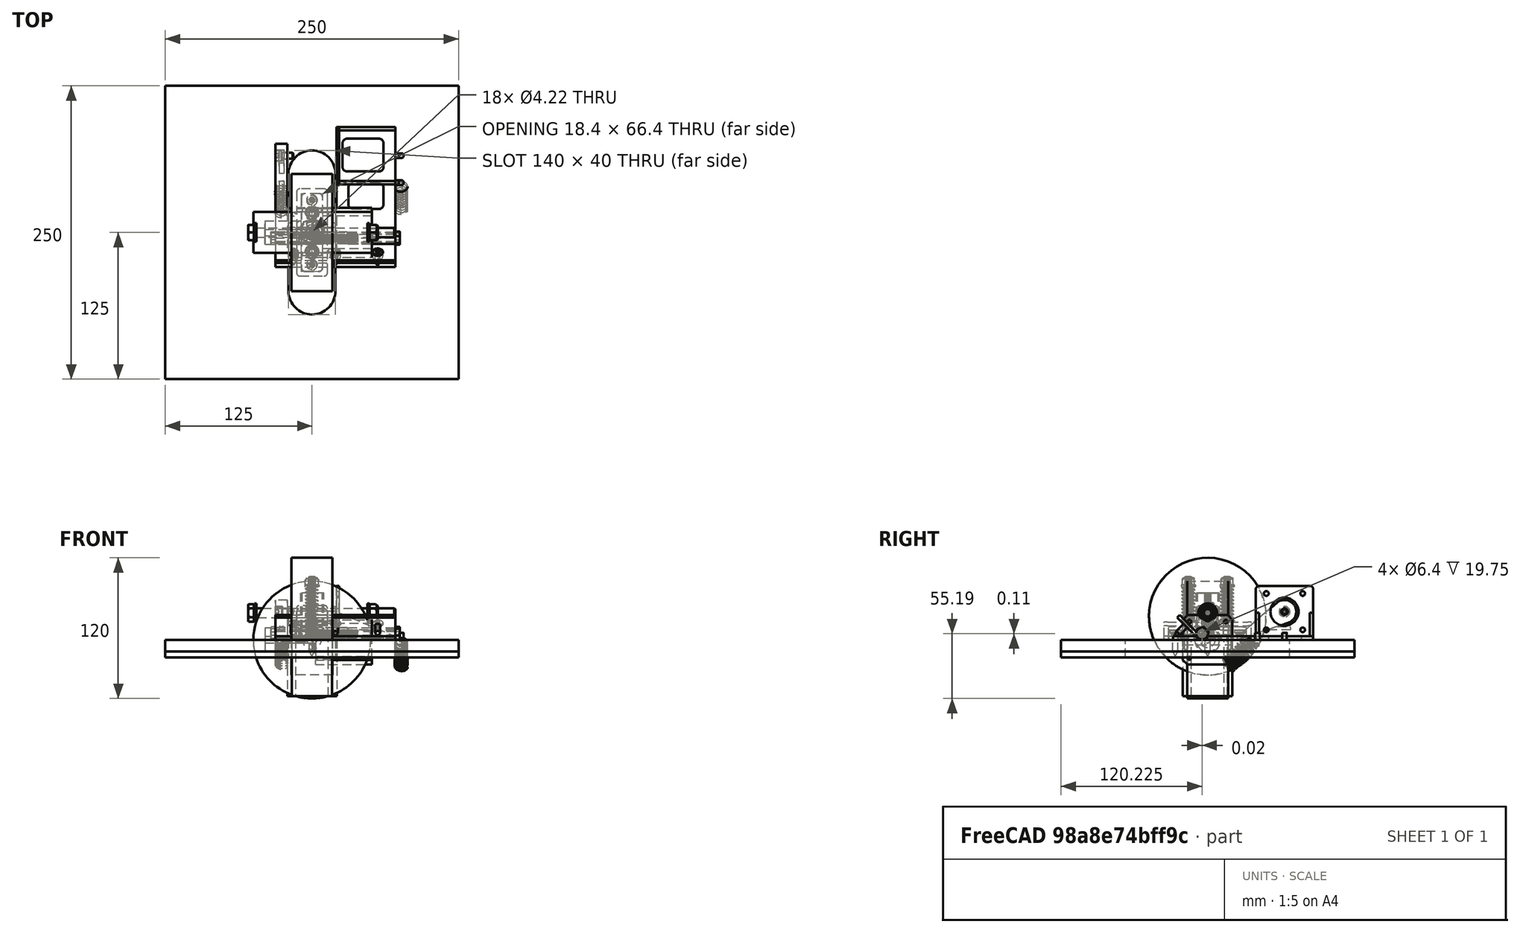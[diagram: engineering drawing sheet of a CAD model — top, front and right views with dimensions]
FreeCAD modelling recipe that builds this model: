
FCSTD DOCUMENT  (FreeCAD 1.0R39285 (Git))
Label: Stirnradantrieb
License: All rights reserved
LicenseURL: https://en.wikipedia.org/wiki/All_rights_reserved
objects: Sketcher::SketchObject×43, PartDesign::Pad×33, Part::FeaturePython×32, Part::Feature×17, PartDesign::Body×13, Mesh::Feature×9, App::Part×6, PartDesign::Pocket×5, PartDesign::Hole×4, PartDesign::Fillet×3, App::DocumentObjectGroup×3, PartDesign::Chamfer×1, App::FeaturePython×1, Assembly::JointGroup×1, PartDesign::AdditiveHelix×1, Assembly::AssemblyObject×1
note: 289 computed .brp shape members not serialized (recipe doc carries the construction recipe); baked Part::Feature solids carry a one-line shape summary decoded from their .brp

FEATURE [Sketcher::SketchObject] Sketch
  ArcFitTolerance = 1e-06
  AttachmentSupport = -> [XY_Plane]
  FullyConstrained = true
  MakeInternals = false
  MapMode = 5
  sketch-geometry (2):
    g0: Circle CenterX=0 CenterY=0 CenterZ=0 NormalX=0 NormalY=0 NormalZ=1 AngleXU=0 Radius=50
    g1: Circle CenterX=0 CenterY=0 CenterZ=0 NormalX=0 NormalY=0 NormalZ=1 AngleXU=0 Radius=4.2
  constraints (4):
    c: Diameter(g0) = 100
    c: Coincident(g0,g-1)
    c: Diameter(g1) = 8.4
    c: Coincident(g1,g0)
FEATURE [PartDesign::Pad] Pad
  Direction = (0,0,1)
  Length = 35
  Length2 = 10
  Midplane = true
  Profile = -> Sketch
  ReferenceAxis = -> Sketch [N_Axis]
  Refine = true
  Suppressed = false
  Type = 0
FEATURE [Sketcher::SketchObject] Sketch001
  ArcFitTolerance = 1e-06
  AttachmentSupport = -> [XY_Plane]
  ExternalGeometry = -> [Pad]
  FullyConstrained = true
  MakeInternals = false
  MapMode = 5
  sketch-geometry (2):
    g0: Circle CenterX=0 CenterY=0 CenterZ=0 NormalX=0 NormalY=0 NormalZ=1 AngleXU=0 Radius=8
    g1: Circle CenterX=0 CenterY=0 CenterZ=0 NormalX=0 NormalY=0 NormalZ=1 AngleXU=0 Radius=4.2
  constraints (4):
    c: Diameter(g0) = 16
    c: Coincident(g0,g-1)
    c: Coincident(g1,g0)
    c: Equal(g1,g-3)
FEATURE [PartDesign::Pad] Pad001
  BaseFeature = -> Pad
  Direction = (0,0,1)
  Length = 40
  Length2 = 10
  Midplane = true
  Profile = -> Sketch001
  ReferenceAxis = -> Sketch001 [N_Axis]
  Refine = true
  Suppressed = false
  Type = 0
FEATURE [PartDesign::Body] Body  label="B-Dummy Rad D100mm"
  AllowCompound = false
  Group = -> [Sketch,Pad,Sketch001,Pad001]
  Origin = -> Origin
  Placement = pos=(0,0,0) rot=(1,0,0;1.5708rad)
  Tip = -> Pad001
FEATURE [Sketcher::SketchObject] Sketch002  label="Sk-Walzenzylinder"
  ArcFitTolerance = 1e-06
  AttachmentSupport = -> [XY_Plane001]
  FullyConstrained = true
  MakeInternals = false
  MapMode = 5
  sketch-geometry (2):
    g0: Circle CenterX=0 CenterY=0 CenterZ=0 NormalX=0 NormalY=0 NormalZ=1 AngleXU=0 Radius=10
    g1: Circle CenterX=0 CenterY=0 CenterZ=0 NormalX=0 NormalY=0 NormalZ=1 AngleXU=0 Radius=2.65
  constraints (4):
    c: Diameter(g0) = 20
    c: Coincident(g0,g-1)
    c: Coincident(g1,g0)
    c: Diameter(g1) = 5.3
FEATURE [PartDesign::Pad] Pad002  label="P-Walzenzylinder"
  Direction = (0,0,1)
  Length = 40
  Length2 = 10
  Profile = -> Sketch002
  ReferenceAxis = -> Sketch002 [N_Axis]
  Refine = true
  Suppressed = false
  Type = 0
FEATURE [Sketcher::SketchObject] Sketch003  label="Sk-Wellenfeder"
  ArcFitTolerance = 1e-06
  AttachmentOffset = pos=(0,0,-5) rot=(0,0,1;0rad)
  AttachmentSupport = -> [Pad002]
  ExternalGeometry = -> [Pad002]
  FullyConstrained = true
  MakeInternals = false
  MapMode = 5
  Placement = pos=(0,0,5) rot=(1,0,0;3.14159rad)
  sketch-geometry (6):
    g0: LineSegment StartX=-1.67929 StartY=2.65 StartZ=0 EndX=-1.67929 EndY=2.05 EndZ=0
    g1: LineSegment StartX=-1.67929 StartY=2.05 StartZ=0 EndX=1.67929 EndY=2.05 EndZ=0
    g2: LineSegment StartX=1.67929 StartY=2.05 StartZ=0 EndX=1.67929 EndY=2.65 EndZ=0
    g3: LineSegment [constr] StartX=0 StartY=2.05 StartZ=0 EndX=0 EndY=-2.65 EndZ=0
    g4: LineSegment StartX=1.67929 StartY=2.65 StartZ=0 EndX=0 EndY=2.65 EndZ=0
    g5: LineSegment StartX=0 StartY=2.65 StartZ=0 EndX=-1.67929 EndY=2.65 EndZ=0
  constraints (19):
    c: Coincident(g0,g1)
    c: Coincident(g1,g2)
    c: Coincident(g2,g4)
    c: Coincident(g5,g0)
    c: Vertical(g0)
    c: Vertical(g2)
    c: Horizontal(g1)
    c: PointOnObject(g3,g-3)
    c: Vertical(g3)
    c: PointOnObject(g-1,g3)
    c: PointOnObject(g1,g-3)
    c: PointOnObject(g0,g-3)
    c: Coincident(g4,g5)
    c: Horizontal(g4)
    c: Horizontal(g5)
    c: PointOnObject(g4,g-3)
    c: Equal(g5,g4)
    c: PointOnObject(g3,g1)
    c: DistanceY(g3,g3) = 4.7
FEATURE [PartDesign::Pad] Pad003  label="P-Walze mit Wellenfeder"
  BaseFeature = -> Pad002
  Direction = (0,0,-1)
  Length = 20
  Length2 = 10
  Profile = -> Sketch003
  ReferenceAxis = -> Sketch003 [N_Axis]
  Refine = true
  Reversed = true
  Suppressed = false
  Type = 0
FEATURE [PartDesign::Chamfer] Chamfer  label="P-Antriebswalze NEMA17"
  Angle = 45
  Base = -> Pad003 [Edge13]
  BaseFeature = -> Pad003
  ChamferType = 0
  FlipDirection = false
  Refine = true
  Size = 0.5
  Size2 = 1
  SupportTransform = false
  Suppressed = false
  UseAllEdges = false
FEATURE [PartDesign::Body] Body001  label="B-Antriebswalze-NEMA17_20.0"
  AllowCompound = false
  Group = -> [Sketch002,Pad002,Sketch003,Pad003,Chamfer]
  Origin = -> Origin001
  Tip = -> Chamfer
FEATURE [Part::Feature] Body002  label="S-Dummy Rad D100"
  Placement = pos=(0.00966072,0.00966072,20) rot=(0.57735,-0.57735,0.57735;4.18879rad)
  shape: bbox 40 x 100 x 100 mm, 8 faces (baked)
FEATURE [Part::Feature] Body003  label="S-Antriebswalze-NEMA17"
  Placement = pos=(0,0,0) rot=(0,-1,0;1.5708rad)
  shape: bbox 40 x 20 x 20 mm, 8 faces (baked)
FEATURE [Sketcher::SketchObject] Sketch004  label="Sk-Stepper NEMA17 Body"
  ArcFitTolerance = 1e-06
  AttachmentSupport = -> [XY_Plane004]
  FullyConstrained = true
  MakeInternals = false
  MapMode = 5
  sketch-geometry (25):
    g0: LineSegment StartX=-21.15 StartY=17.15 StartZ=0 EndX=-21.15 EndY=-17.15 EndZ=0
    g1: LineSegment StartX=-17.15 StartY=-21.15 StartZ=0 EndX=17.15 EndY=-21.15 EndZ=0
    g2: LineSegment StartX=21.15 StartY=-17.15 StartZ=0 EndX=21.15 EndY=17.15 EndZ=0
    g3: LineSegment StartX=17.15 StartY=21.15 StartZ=0 EndX=-17.15 EndY=21.15 EndZ=0
    g4: LineSegment StartX=-21.15 StartY=17.15 StartZ=0 EndX=-17.15 EndY=21.15 EndZ=0
    g5: LineSegment StartX=17.15 StartY=21.15 StartZ=0 EndX=21.15 EndY=17.15 EndZ=0
    g6: LineSegment StartX=21.15 StartY=-17.15 StartZ=0 EndX=17.15 EndY=-21.15 EndZ=0
    g7: LineSegment StartX=-17.15 StartY=-21.15 StartZ=0 EndX=-21.15 EndY=-17.15 EndZ=0
    g8: LineSegment [constr] StartX=-21.15 StartY=17.15 StartZ=0 EndX=-17.15 EndY=17.15 EndZ=0
    g9: LineSegment [constr] StartX=-17.15 StartY=17.15 StartZ=0 EndX=-17.15 EndY=21.15 EndZ=0
    g10: LineSegment [constr] StartX=21.15 StartY=-17.15 StartZ=0 EndX=17.15 EndY=-17.15 EndZ=0
    g11: LineSegment [constr] StartX=17.15 StartY=-17.15 StartZ=0 EndX=17.15 EndY=-21.15 EndZ=0
    g12: LineSegment [constr] StartX=17.15 StartY=17.15 StartZ=0 EndX=21.15 EndY=17.15 EndZ=0
    g13: LineSegment [constr] StartX=17.15 StartY=17.15 StartZ=0 EndX=17.15 EndY=21.15 EndZ=0
    g14: LineSegment [constr] StartX=-17.15 StartY=-17.15 StartZ=0 EndX=-17.15 EndY=-21.15 EndZ=0
    g15: LineSegment [constr] StartX=-17.15 StartY=-17.15 StartZ=0 EndX=-21.15 EndY=-17.15 EndZ=0
    g16: LineSegment [constr] StartX=-15.5 StartY=-15.5 StartZ=0 EndX=15.5 EndY=-15.5 EndZ=0
    g17: LineSegment [constr] StartX=15.5 StartY=-15.5 StartZ=0 EndX=15.5 EndY=15.5 EndZ=0
    g18: LineSegment [constr] StartX=15.5 StartY=15.5 StartZ=0 EndX=-15.5 EndY=15.5 EndZ=0
    g19: LineSegment [constr] StartX=-15.5 StartY=15.5 StartZ=0 EndX=-15.5 EndY=-15.5 EndZ=0
    g20: GeomPoint [constr] X=0 Y=0 Z=0
    g21: Circle CenterX=-15.5 CenterY=15.5 CenterZ=0 NormalX=0 NormalY=0 NormalZ=1 AngleXU=0 Radius=1.5
    g22: Circle CenterX=15.5 CenterY=15.5 CenterZ=0 NormalX=0 NormalY=0 NormalZ=1 AngleXU=0 Radius=1.5
    g23: Circle CenterX=15.5 CenterY=-15.5 CenterZ=0 NormalX=0 NormalY=0 NormalZ=1 AngleXU=0 Radius=1.5
    g24: Circle CenterX=-15.5 CenterY=-15.5 CenterZ=0 NormalX=0 NormalY=0 NormalZ=1 AngleXU=0 Radius=1.5
  constraints (62):
    c: Vertical(g2)
    c: Horizontal(g1)
    c: Coincident(g4,g0)
    c: Coincident(g4,g3)
    c: Coincident(g5,g3)
    c: Coincident(g5,g2)
    c: Coincident(g6,g2)
    c: Coincident(g6,g1)
    c: Coincident(g7,g1)
    c: Coincident(g7,g0)
    c: Equal(g3,g2)
    c: Equal(g4,g5)
    c: Equal(g5,g6)
    c: Equal(g6,g7)
    c: DistanceX(g0,g2) = 42.3
    c: Coincident(g8,g0)
    c: Horizontal(g8)
    c: Coincident(g9,g8)
    c: Coincident(g9,g3)
    c: Coincident(g10,g2)
    c: Coincident(g11,g10)
    c: Coincident(g11,g1)
    c: Vertical(g11)
    c: Equal(g11,g10)
    c: Horizontal(g10)
    c: Equal(g8,g9)
    c: Vertical(g9)
    c: Coincident(g13,g3)
    c: Coincident(g14,g1)
    c: Coincident(g15,g0)
    c: Coincident(g12,g2)
    c: Vertical(g13)
    c: Vertical(g14)
    c: Coincident(g12,g13)
    c: Coincident(g14,g15)
    c: Horizontal(g15)
    c: Equal(g15,g14)
    c: Equal(g13,g12)
    c: Horizontal(g12)
    c: DistanceX(g8,g8) = 4
    c: Symmetric(g3,g3,g-2)
    c: Symmetric(g0,g0,g-1)
    c: Coincident(g16,g17)
    c: Coincident(g17,g18)
    c: Coincident(g18,g19)
    c: Coincident(g19,g16)
    c: Horizontal(g16)
    c: Horizontal(g18)
    c: Vertical(g17)
    c: Vertical(g19)
    c: Symmetric(g18,g16,g20)
    c: Coincident(g20,g-1)
    c: DistanceX(g18,g18) = 31
    c: Equal(g18,g17)
    c: Coincident(g21,g18)
    c: Coincident(g22,g17)
    c: Coincident(g23,g16)
    c: Coincident(g24,g16)
    c: Diameter(g21) = 3
    c: Equal(g21,g22)
    c: Equal(g22,g23)
    c: Equal(g23,g24)
FEATURE [PartDesign::Pad] Pad004  label="P-Stepper NEMA17 1"
  Direction = (0,0,1)
  Length = 48
  Length2 = 10
  Profile = -> Sketch004
  ReferenceAxis = -> Sketch004 [N_Axis]
  Refine = true
  Reversed = true
  Suppressed = false
  Type = 0
FEATURE [Sketcher::SketchObject] Sketch005  label="Sk-Stepper NEMA17 Centerring"
  ArcFitTolerance = 1e-06
  AttachmentSupport = -> [Pad004]
  FullyConstrained = true
  MakeInternals = false
  MapMode = 5
  sketch-geometry (2):
    g0: Circle CenterX=0 CenterY=0 CenterZ=0 NormalX=0 NormalY=0 NormalZ=1 AngleXU=0 Radius=6.5
    g1: Circle CenterX=0 CenterY=0 CenterZ=0 NormalX=0 NormalY=0 NormalZ=1 AngleXU=0 Radius=11
  constraints (4):
    c: Diameter(g0) = 13
    c: Coincident(g0,g-1)
    c: Diameter(g1) = 22
    c: Coincident(g1,g0)
FEATURE [PartDesign::Pad] Pad005  label="P-Stepper NEMA17 2"
  BaseFeature = -> Pad004
  Direction = (0,0,1)
  Length = 2
  Length2 = 10
  Profile = -> Sketch005
  ReferenceAxis = -> Sketch005 [N_Axis]
  Refine = true
  Suppressed = false
  Type = 0
FEATURE [Sketcher::SketchObject] Sketch006  label="Sk-Stepper NEMA17 Welle"
  ArcFitTolerance = 1e-06
  AttachmentSupport = -> [Pad005]
  FullyConstrained = true
  MakeInternals = false
  MapMode = 5
  sketch-geometry (1):
    g0: Circle CenterX=0 CenterY=0 CenterZ=0 NormalX=0 NormalY=0 NormalZ=1 AngleXU=0 Radius=2.5
  constraints (2):
    c: Diameter(g0) = 5
    c: Coincident(g0,g-1)
FEATURE [PartDesign::Pad] Pad006  label="P-Stepper NEMA17 dummy"
  BaseFeature = -> Pad005
  Direction = (0,0,1)
  Length = 24
  Length2 = 10
  Profile = -> Sketch006
  ReferenceAxis = -> Sketch006 [N_Axis]
  Refine = true
  Suppressed = false
  Type = 0
FEATURE [PartDesign::Body] Body004  label="B-Dummy Stepper NEMA17"
  AllowCompound = false
  Group = -> [Sketch004,Pad004,Sketch005,Pad005,Sketch006,Pad006]
  Origin = -> Origin004
  Tip = -> Pad006
FEATURE [Part::Feature] Body005  label="S-Dummy Stepper NEMA17"
  Placement = pos=(3,0,0) rot=(0,1,0;-1.5708rad)
  shape: bbox 72 x 42.3 x 42.3 mm, 20 faces (baked)
FEATURE [App::Part] Part  label="Stepper Antrieb"
  Group = -> [Body003,Body005]
  Origin = -> Origin005
  Placement = pos=(20,65.5,24.15) rot=(1,0,0;0rad)
FEATURE [Mesh::Feature] Mesh  label="M-Antriebswalze-NEMA17"
FEATURE [Sketcher::SketchObject] Sketch007  label="Sk Rotationsplatter"
  ArcFitTolerance = 1e-06
  AttachmentSupport = -> [XY_Plane006]
  FullyConstrained = true
  MakeInternals = false
  MapMode = 5
  sketch-geometry (8):
    g0: LineSegment StartX=-125 StartY=125 StartZ=0 EndX=-125 EndY=-125 EndZ=0
    g1: LineSegment StartX=-125 StartY=-125 StartZ=0 EndX=125 EndY=-125 EndZ=0
    g2: LineSegment StartX=125 StartY=-125 StartZ=0 EndX=125 EndY=125 EndZ=0
    g3: LineSegment StartX=125 StartY=125 StartZ=0 EndX=-125 EndY=125 EndZ=0
    g4: ArcOfCircle CenterX=0 CenterY=50 CenterZ=0 NormalX=0 NormalY=0 NormalZ=1 AngleXU=0 Radius=20 StartAngle=-9e-16 EndAngle=3.14159
    g5: ArcOfCircle CenterX=0 CenterY=-50 CenterZ=0 NormalX=0 NormalY=0 NormalZ=1 AngleXU=0 Radius=20 StartAngle=3.14159 EndAngle=6.28319
    g6: LineSegment StartX=20 StartY=50 StartZ=0 EndX=20 EndY=-50 EndZ=0
    g7: LineSegment StartX=-20 StartY=50 StartZ=0 EndX=-20 EndY=-50 EndZ=0
  constraints (20):
    c: Coincident(g0,g1)
    c: Coincident(g1,g2)
    c: Coincident(g2,g3)
    c: Coincident(g3,g0)
    c: Vertical(g0)
    c: Vertical(g2)
    c: Horizontal(g1)
    c: Horizontal(g3)
    c: Symmetric(g2,g0,g-1)
    c: DistanceY(g2,g2) = 250
    c: DistanceX(g3,g3) = 250
    c: Tangent(g4,g6) = 1.5708
    c: Tangent(g4,g7) = -1.5708
    c: Tangent(g5,g6) = 1.5708
    c: Tangent(g5,g7) = -1.5708
    c: Equal(g4,g5)
    c: PointOnObject(g4,g-2)
    c: Diameter(g4) = 40
    c: Symmetric(g4,g5,g-1)
    c: DistanceY(g5,g4) = 100
FEATURE [PartDesign::Pad] Pad007  label="P-Rotationsplatte"
  Direction = (0,0,1)
  Length = 15
  Length2 = 10
  Profile = -> Sketch007
  ReferenceAxis = -> Sketch007 [N_Axis]
  Refine = true
  Reversed = true
  Suppressed = false
  Type = 0
FEATURE [PartDesign::Body] Body006  label="B-Dummy Rotationsplatte"
  AllowCompound = false
  Group = -> [Sketch007,Pad007]
  Origin = -> Origin006
  Tip = -> Pad007
FEATURE [Sketcher::SketchObject] Sketch008  label="Sk Grundplatte"
  ArcFitTolerance = 1e-06
  AttachmentSupport = -> [XY_Plane008]
  FullyConstrained = true
  MakeInternals = false
  MapMode = 5
  sketch-geometry (5):
    g0: LineSegment StartX=-125 StartY=-125 StartZ=0 EndX=125 EndY=-125 EndZ=0
    g1: LineSegment StartX=125 StartY=-125 StartZ=0 EndX=125 EndY=125 EndZ=0
    g2: LineSegment StartX=125 StartY=125 StartZ=0 EndX=-125 EndY=125 EndZ=0
    g3: LineSegment StartX=-125 StartY=125 StartZ=0 EndX=-125 EndY=-125 EndZ=0
    g4: GeomPoint [constr] X=0 Y=0 Z=0
  constraints (12):
    c: Coincident(g0,g1)
    c: Coincident(g1,g2)
    c: Coincident(g2,g3)
    c: Coincident(g3,g0)
    c: Horizontal(g0)
    c: Horizontal(g2)
    c: Vertical(g1)
    c: Vertical(g3)
    c: Symmetric(g2,g0,g4)
    c: Distance(g1,g3) = 250
    c: Distance(g0,g2) = 250
    c: Coincident(g4,g-1)
FEATURE [PartDesign::Pad] Pad008
  Direction = (0,0,1)
  Length = 10
  Length2 = 10
  Profile = -> Sketch008
  ReferenceAxis = -> Sketch008 [N_Axis]
  Refine = true
  Reversed = true
  Suppressed = false
  Type = 0
FEATURE [PartDesign::Body] Body008  label="B-Dummy Grundplatte"
  AllowCompound = false
  Group = -> [Sketch008,Pad008]
  Origin = -> Origin008
  Tip = -> Pad008
FEATURE [Part::Feature] Body009  label="S-Dummy Grundplatte"
  shape: bbox 250 x 250 x 10 mm, 6 faces (baked)
FEATURE [Part::Feature] Body010  label="S-Dummy Rotationsplatte"
  shape: bbox 250 x 250 x 15 mm, 10 faces (baked)
FEATURE [Sketcher::SketchObject] Sketch009  label="Sk-Radlagerbasis Boden"
  ArcFitTolerance = 1e-06
  AttachmentSupport = -> [XY_Plane010]
  FullyConstrained = true
  MakeInternals = false
  MapMode = 5
  sketch-geometry (46):
    g0: LineSegment StartX=-9 StartY=30 StartZ=0 EndX=-9 EndY=-30 EndZ=0
    g1: LineSegment StartX=-6 StartY=-33 StartZ=0 EndX=6 EndY=-33 EndZ=0
    g2: LineSegment StartX=9 StartY=-30 StartZ=0 EndX=9 EndY=30 EndZ=0
    g3: LineSegment StartX=6 StartY=33 StartZ=0 EndX=-6 EndY=33 EndZ=0
    g4: ArcOfCircle CenterX=-6 CenterY=30 CenterZ=0 NormalX=0 NormalY=0 NormalZ=1 AngleXU=0 Radius=3 StartAngle=1.5708 EndAngle=3.14159
    g5: ArcOfCircle CenterX=-6 CenterY=-30 CenterZ=0 NormalX=0 NormalY=0 NormalZ=1 AngleXU=0 Radius=3 StartAngle=3.14159 EndAngle=4.71239
    g6: ArcOfCircle CenterX=6 CenterY=-30 CenterZ=0 NormalX=0 NormalY=0 NormalZ=1 AngleXU=0 Radius=3 StartAngle=4.71239 EndAngle=6.28319
    g7: ArcOfCircle CenterX=6 CenterY=30 CenterZ=0 NormalX=0 NormalY=0 NormalZ=1 AngleXU=0 Radius=3 StartAngle=0 EndAngle=1.5708
    g8: GeomPoint [constr] X=-9 Y=33 Z=0
    g9: GeomPoint [constr] X=9 Y=-33 Z=0
    g10: LineSegment StartX=3.00222 StartY=11.3 StartZ=0 EndX=6.00444 EndY=16.5 EndZ=0
    g11: LineSegment StartX=6.00444 StartY=16.5 StartZ=0 EndX=3.00222 EndY=21.7 EndZ=0
    g12: LineSegment StartX=3.00222 StartY=21.7 StartZ=0 EndX=-3.00222 EndY=21.7 EndZ=0
    g13: LineSegment StartX=-3.00222 StartY=21.7 StartZ=0 EndX=-6.00444 EndY=16.5 EndZ=0
    g14: LineSegment StartX=-6.00444 StartY=16.5 StartZ=0 EndX=-3.00222 EndY=11.3 EndZ=0
    g15: LineSegment StartX=-3.00222 StartY=11.3 StartZ=0 EndX=3.00222 EndY=11.3 EndZ=0
    g16: Circle [constr] CenterX=0 CenterY=16.5 CenterZ=0 NormalX=0 NormalY=0 NormalZ=1 AngleXU=0 Radius=6.00444
    g17: LineSegment StartX=-3.00222 StartY=-21.7 StartZ=0 EndX=3.00222 EndY=-21.7 EndZ=0
    g18: LineSegment StartX=3.00222 StartY=-21.7 StartZ=0 EndX=6.00444 EndY=-16.5 EndZ=0
    g19: LineSegment StartX=6.00444 StartY=-16.5 StartZ=0 EndX=3.00222 EndY=-11.3 EndZ=0
    g20: LineSegment StartX=3.00222 StartY=-11.3 StartZ=0 EndX=-3.00222 EndY=-11.3 EndZ=0
    g21: LineSegment StartX=-3.00222 StartY=-11.3 StartZ=0 EndX=-6.00444 EndY=-16.5 EndZ=0
    g22: LineSegment StartX=-6.00444 StartY=-16.5 StartZ=0 EndX=-3.00222 EndY=-21.7 EndZ=0
    g23: Circle [constr] CenterX=0 CenterY=-16.5 CenterZ=0 NormalX=0 NormalY=0 NormalZ=1 AngleXU=0 Radius=6.00444
    g24: LineSegment [constr] StartX=0 StartY=16.5 StartZ=0 EndX=0 EndY=-16.5 EndZ=0
    g25: Circle CenterX=0 CenterY=27.5 CenterZ=0 NormalX=0 NormalY=0 NormalZ=1 AngleXU=0 Radius=2.5
    g26: Circle CenterX=0 CenterY=-27.5 CenterZ=0 NormalX=0 NormalY=0 NormalZ=1 AngleXU=0 Radius=2.5
    g27: Circle CenterX=0 CenterY=0 CenterZ=0 NormalX=0 NormalY=0 NormalZ=1 AngleXU=0 Radius=2.5
    g28: LineSegment [constr] StartX=0 StartY=27.5 StartZ=0 EndX=0 EndY=30 EndZ=0
    g29: LineSegment [constr] StartX=0 StartY=30 StartZ=0 EndX=0 EndY=33 EndZ=0
    g30: LineSegment [constr] StartX=0 StartY=-27.5 StartZ=0 EndX=0 EndY=-30 EndZ=0
    g31: LineSegment [constr] StartX=0 StartY=-30 StartZ=0 EndX=0 EndY=-33 EndZ=0
    g32: Circle [constr] CenterX=0 CenterY=16.5 CenterZ=0 NormalX=0 NormalY=0 NormalZ=1 AngleXU=0 Radius=6.00444
    g33: Circle [constr] CenterX=0 CenterY=16.5 CenterZ=0 NormalX=0 NormalY=0 NormalZ=1 AngleXU=0 Radius=6.00444
    g34: Circle [constr] CenterX=0 CenterY=16.5 CenterZ=0 NormalX=0 NormalY=0 NormalZ=1 AngleXU=0 Radius=8.5
    g35: Circle [constr] CenterX=0 CenterY=-16.5 CenterZ=0 NormalX=0 NormalY=0 NormalZ=1 AngleXU=0 Radius=8.5
    g36: LineSegment [constr] StartX=-5 StartY=-8 StartZ=0 EndX=5 EndY=-8 EndZ=0
    g37: LineSegment [constr] StartX=5 StartY=-8 StartZ=0 EndX=5 EndY=8 EndZ=0
    g38: LineSegment [constr] StartX=5 StartY=8 StartZ=0 EndX=-5 EndY=8 EndZ=0
    g39: LineSegment [constr] StartX=-5 StartY=8 StartZ=0 EndX=-5 EndY=-8 EndZ=0
    g40: GeomPoint [constr] X=0 Y=0 Z=0
    g41: GeomPoint [constr] X=0 Y=25 Z=0
    g42: GeomPoint [constr] X=0 Y=8 Z=0
    g43: GeomPoint [constr] X=0 Y=-8 Z=0
    g44: GeomPoint [constr] X=0 Y=-25 Z=0
    g45: LineSegment [constr] StartX=-6.00444 StartY=16.5 StartZ=0 EndX=-9 EndY=16.5 EndZ=0
  constraints (112):
    c: Tangent(g0,g4) = -1.5708
    c: Tangent(g0,g5) = -1.5708
    c: Tangent(g1,g5) = -1.5708
    c: Tangent(g1,g6) = -1.5708
    c: Tangent(g2,g6) = -1.5708
    c: Tangent(g2,g7) = -1.5708
    c: Tangent(g3,g7) = -1.5708
    c: Tangent(g3,g4) = -1.5708
    c: Vertical(g0)
    c: Vertical(g2)
    c: Horizontal(g1)
    c: Horizontal(g3)
    c: Equal(g4,g5)
    c: Equal(g5,g6)
    c: Equal(g6,g7)
    c: PointOnObject(g8,g0)
    c: PointOnObject(g8,g3)
    c: PointOnObject(g9,g1)
    c: PointOnObject(g9,g2)
    c: Radius(g5) = 3
    c: Symmetric(g8,g9,g-1)
    c: DistanceX(g0,g2) = 18
    c: DistanceY(g1,g3) = 66
    c: Coincident(g10,g11)
    c: Coincident(g11,g12)
    c: Coincident(g12,g13)
    c: Coincident(g13,g14)
    c: Coincident(g14,g15)
    c: Coincident(g15,g10)
    c: Equal(g10, g11-g15) x5
    c: PointOnObject(g10,g16)
    c: PointOnObject(g12,g16)
    c: PointOnObject(g13,g16)
    c: PointOnObject(g14,g16)
    c: PointOnObject(g15,g16)
    c: PointOnObject(g16,g-2)
    c: Coincident(g17,g18)
    c: Coincident(g18,g19)
    c: Coincident(g19,g20)
    c: Coincident(g20,g21)
    c: Coincident(g21,g22)
    c: Coincident(g22,g17)
    c: Equal(g17, g18-g22) x5
    c: PointOnObject(g17,g23)
    c: PointOnObject(g18,g23)
    c: PointOnObject(g19,g23)
    c: PointOnObject(g20,g23)
    c: PointOnObject(g21,g23)
    c: Equal(g16,g23)
    c: Coincident(g24,g16)
    c: Coincident(g24,g23)
    c: Symmetric(g23,g16,g-1)
    c: Diameter(g25) = 5
    c: PointOnObject(g25,g-2)
    c: PointOnObject(g26,g-2)
    c: Coincident(g27,g-1)
    c: Equal(g25,g27)
    c: Equal(g27,g26)
    c: Coincident(g30,g26)
    c: PointOnObject(g31,g1)
    c: Coincident(g28,g29)
    c: Vertical(g28)
    c: Vertical(g29)
    c: PointOnObject(g28,g25)
    c: Coincident(g25,g28)
    c: DistanceY(g29,g29) = 3
    c: Coincident(g30,g31)
    c: Vertical(g30)
    c: Vertical(g31)
    c: PointOnObject(g30,g26)
    c: Equal(g31,g29)
    c: Coincident(g32,g16)
    c: PointOnObject(g10,g32)
    c: Coincident(g33,g16)
    c: PointOnObject(g10,g33)
    c: Coincident(g34,g16)
    c: Diameter(g34) = 17
    c: Coincident(g35,g23)
    c: Equal(g34,g35)
    c: Coincident(g36,g37)
    c: Coincident(g37,g38)
    c: Coincident(g38,g39)
    c: Coincident(g39,g36)
    c: Horizontal(g36)
    c: Horizontal(g38)
    c: Vertical(g37)
    c: Vertical(g39)
    c: Symmetric(g38,g36,g40)
    c: Distance(g37,g39) = 10
    c: Distance(g36,g38) = 16
    c: Coincident(g40,g27)
    c: PointOnObject(g41,g34)
    c: PointOnObject(g43,g35)
    c: PointOnObject(g44,g35)
    c: PointOnObject(g44,g26)
    c: PointOnObject(g44,g-2)
    c: PointOnObject(g41,g25)
    c: PointOnObject(g41,g-2)
    c: PointOnObject(g42,g34)
    c: PointOnObject(g42,g24)
    c: PointOnObject(g43,g24)
    c: PointOnObject(g42,g38)
    c: DistanceY(g11,g41) = 3.3
    c: PointOnObject(g11,g16)
    c: Horizontal(g12)
    c: DistanceY(g14,g12) = 10.4
    c: PointOnObject(g17,g23)
    c: Horizontal(g20)
    c: Coincident(g45,g13)
    c: PointOnObject(g45,g0)
    c: Horizontal(g45)
    c: DistanceX(g45,g45) = 2.99556
FEATURE [PartDesign::Pad] Pad009  label="P-Radlagerbasis 1"
  Direction = (0,0,1)
  Length = 4.2
  Length2 = 10
  Profile = -> Sketch009
  ReferenceAxis = -> Sketch009 [N_Axis]
  Refine = true
  Suppressed = false
  Type = 0
FEATURE [Sketcher::SketchObject] Sketch010  label="Sk-Radlagerbasis Deckel"
  ArcFitTolerance = 1e-06
  AttachmentSupport = -> [Pad009]
  ExternalGeometry = -> [Pad009]
  FullyConstrained = true
  MakeInternals = false
  MapMode = 5
  Placement = pos=(0,0,4.2) rot=(0,0,1;0rad)
  sketch-geometry (21):
    g0: LineSegment StartX=-9 StartY=30 StartZ=0 EndX=-9 EndY=-30 EndZ=0
    g1: LineSegment StartX=-6 StartY=-33 StartZ=0 EndX=6 EndY=-33 EndZ=0
    g2: LineSegment StartX=9 StartY=-30 StartZ=0 EndX=9 EndY=30 EndZ=0
    g3: LineSegment StartX=6 StartY=33 StartZ=0 EndX=-6 EndY=33 EndZ=0
    g4: ArcOfCircle CenterX=-6 CenterY=30 CenterZ=0 NormalX=0 NormalY=0 NormalZ=1 AngleXU=0 Radius=3 StartAngle=1.5708 EndAngle=3.14159
    g5: ArcOfCircle CenterX=-6 CenterY=-30 CenterZ=0 NormalX=0 NormalY=0 NormalZ=1 AngleXU=0 Radius=3 StartAngle=3.14159 EndAngle=4.71239
    g6: ArcOfCircle CenterX=6 CenterY=-30 CenterZ=0 NormalX=0 NormalY=0 NormalZ=1 AngleXU=0 Radius=3 StartAngle=4.71239 EndAngle=6.28319
    g7: ArcOfCircle CenterX=6 CenterY=30 CenterZ=0 NormalX=0 NormalY=0 NormalZ=1 AngleXU=0 Radius=3 StartAngle=3e-16 EndAngle=1.5708
    g8: GeomPoint [constr] X=-9 Y=33 Z=0
    g9: GeomPoint [constr] X=9 Y=-33 Z=0
    g10: Circle CenterX=0 CenterY=27.5 CenterZ=0 NormalX=0 NormalY=0 NormalZ=1 AngleXU=0 Radius=2.5
    g11: Circle CenterX=0 CenterY=0 CenterZ=0 NormalX=0 NormalY=0 NormalZ=1 AngleXU=0 Radius=2.5
    g12: Circle CenterX=0 CenterY=-27.5 CenterZ=0 NormalX=0 NormalY=0 NormalZ=1 AngleXU=0 Radius=2.5
    g13: LineSegment [constr] StartX=-3.00222 StartY=-11.3 StartZ=0 EndX=3.00222 EndY=-21.7 EndZ=0
    g14: LineSegment [constr] StartX=3.00222 StartY=-11.3 StartZ=0 EndX=-3.00222 EndY=-21.7 EndZ=0
    g15: LineSegment [constr] StartX=-3.00222 StartY=21.7 StartZ=0 EndX=3.00222 EndY=11.3 EndZ=0
    g16: LineSegment [constr] StartX=3.00222 StartY=21.7 StartZ=0 EndX=-3.00222 EndY=11.3 EndZ=0
    g17: GeomPoint [constr] X=-6e-16 Y=16.5 Z=0
    g18: GeomPoint [constr] X=5e-16 Y=-16.5 Z=0
    g19: Circle CenterX=-6e-16 CenterY=16.5 CenterZ=0 NormalX=0 NormalY=0 NormalZ=1 AngleXU=0 Radius=3.15
    g20: Circle CenterX=5e-16 CenterY=-16.5 CenterZ=0 NormalX=0 NormalY=0 NormalZ=1 AngleXU=0 Radius=3.15
  constraints (44):
    c: Tangent(g0,g4) = -1.5708
    c: Tangent(g0,g5) = -1.5708
    c: Tangent(g1,g5) = -1.5708
    c: Tangent(g1,g6) = -1.5708
    c: Tangent(g2,g6) = -1.5708
    c: Tangent(g2,g7) = -1.5708
    c: Tangent(g3,g7) = -1.5708
    c: Tangent(g3,g4) = -1.5708
    c: Vertical(g0)
    c: Vertical(g2)
    c: Horizontal(g1)
    c: Horizontal(g3)
    c: Equal(g4,g5)
    c: Equal(g5,g6)
    c: Equal(g6,g7)
    c: PointOnObject(g8,g0)
    c: PointOnObject(g8,g3)
    c: PointOnObject(g9,g1)
    c: PointOnObject(g9,g2)
    c: Coincident(g3,g-3)
    c: Equal(g4,g-3)
    c: Coincident(g1,g-7)
    c: Coincident(g10,g-4)
    c: Coincident(g11,g-1)
    c: Coincident(g12,g-6)
    c: Equal(g12,g-6)
    c: Equal(g11,g-5)
    c: Equal(g10,g-4)
    c: Coincident(g13,g-10)
    c: Coincident(g13,g-11)
    c: Coincident(g14,g-10)
    c: Coincident(g14,g-11)
    c: Coincident(g15,g-8)
    c: Coincident(g15,g-9)
    c: Coincident(g16,g-8)
    c: Coincident(g16,g-9)
    c: PointOnObject(g17,g15)
    c: PointOnObject(g18,g13)
    c: PointOnObject(g18,g14)
    c: PointOnObject(g17,g16)
    c: Diameter(g19) = 6.3
    c: Coincident(g19,g17)
    c: Coincident(g20,g18)
    c: Equal(g19,g20)
FEATURE [PartDesign::Pad] Pad010  label="P-Radlagerbasis 2"
  BaseFeature = -> Pad009
  Direction = (0,0,1)
  Length = 4
  Length2 = 10
  Profile = -> Sketch010
  ReferenceAxis = -> Sketch010 [N_Axis]
  Refine = true
  Suppressed = false
  Type = 0
FEATURE [Sketcher::SketchObject] Sketch011  label="Sk-Radlagerbasis Schraublöcher"
  ArcFitTolerance = 1e-06
  AttachmentSupport = -> [Pad010]
  ExternalGeometry = -> [Pad010]
  FullyConstrained = true
  MakeInternals = false
  MapMode = 5
  Placement = pos=(0,0,8.2) rot=(0,0,1;0rad)
  sketch-geometry (3):
    g0: Circle CenterX=0 CenterY=0 CenterZ=0 NormalX=0 NormalY=0 NormalZ=1 AngleXU=0 Radius=2.5
    g1: Circle CenterX=0 CenterY=-27.5 CenterZ=0 NormalX=0 NormalY=0 NormalZ=1 AngleXU=0 Radius=2.5
    g2: Circle CenterX=0 CenterY=27.5 CenterZ=0 NormalX=0 NormalY=0 NormalZ=1 AngleXU=0 Radius=2.5
  constraints (6):
    c: Coincident(g0,g-1)
    c: Coincident(g1,g-5)
    c: Equal(g1,g-5)
    c: Coincident(g2,g-4)
    c: Equal(g2,g-4)
    c: Equal(g-3,g0)
FEATURE [PartDesign::Hole] Hole  label="P-Radlagerbasis 3"
  BaseFeature = -> Pad010
  CustomThreadClearance = 0
  Depth = 2
  DepthType = 0
  Diameter = 9.2
  DrillForDepth = false
  DrillPoint = 1
  DrillPointAngle = 90
  HoleCutCountersinkAngle = 90
  HoleCutCustomValues = false
  HoleCutDepth = 0
  HoleCutDiameter = 15.8
  HoleCutType = 0
  ModelThread = false
  Profile = -> Sketch011
  Refine = true
  Suppressed = false
  Tapered = false
  TaperedAngle = 77
  ThreadClass = 0
  ThreadDepth = 2
  ThreadDepthType = 0
  ThreadDirection = 0
  ThreadFit = 0
  ThreadSize = 0
  ThreadType = 0
  Threaded = false
  UseCustomThreadClearance = false
FEATURE [PartDesign::Body] Body011  label="B-Radlagerbasis"
  AllowCompound = false
  Group = -> [Sketch009,Pad009,Sketch010,Pad010,Sketch011,Hole]
  Origin = -> Origin010
  Tip = -> Hole
FEATURE [Sketcher::SketchObject] Sketch015  label="Sk-Radlagerfeder Boden"
  ArcFitTolerance = 1e-06
  AttachmentSupport = -> [XY_Plane011]
  FullyConstrained = true
  MakeInternals = false
  MapMode = 5
  sketch-geometry (23):
    g0: LineSegment StartX=-9.2 StartY=30 StartZ=0 EndX=-9.2 EndY=-30 EndZ=0
    g1: LineSegment StartX=-6 StartY=-33.2 StartZ=0 EndX=6 EndY=-33.2 EndZ=0
    g2: LineSegment StartX=9.2 StartY=-30 StartZ=0 EndX=9.2 EndY=30 EndZ=0
    g3: LineSegment StartX=6 StartY=33.2 StartZ=0 EndX=-6 EndY=33.2 EndZ=0
    g4: ArcOfCircle CenterX=-6 CenterY=30 CenterZ=0 NormalX=0 NormalY=0 NormalZ=1 AngleXU=0 Radius=3.2 StartAngle=1.5708 EndAngle=3.14159
    g5: ArcOfCircle CenterX=-6 CenterY=-30 CenterZ=0 NormalX=0 NormalY=0 NormalZ=1 AngleXU=0 Radius=3.2 StartAngle=3.14159 EndAngle=4.71239
    g6: ArcOfCircle CenterX=6 CenterY=-30 CenterZ=0 NormalX=0 NormalY=0 NormalZ=1 AngleXU=0 Radius=3.2 StartAngle=4.71239 EndAngle=6.28319
    g7: ArcOfCircle CenterX=6 CenterY=30 CenterZ=0 NormalX=0 NormalY=0 NormalZ=1 AngleXU=0 Radius=3.2 StartAngle=0 EndAngle=1.5708
    g8: GeomPoint [constr] X=-9.2 Y=33.2 Z=0
    g9: GeomPoint [constr] X=9.2 Y=-33.2 Z=0
    g10: GeomPoint [constr] X=0 Y=0 Z=0
    g11: LineSegment StartX=-13.2 StartY=34.2 StartZ=0 EndX=-13.2 EndY=-34.2 EndZ=0
    g12: LineSegment StartX=-10.2 StartY=-37.2 StartZ=0 EndX=10.2 EndY=-37.2 EndZ=0
    g13: LineSegment StartX=13.2 StartY=-34.2 StartZ=0 EndX=13.2 EndY=34.2 EndZ=0
    g14: LineSegment StartX=10.2 StartY=37.2 StartZ=0 EndX=-10.2 EndY=37.2 EndZ=0
    g15: ArcOfCircle CenterX=-10.2 CenterY=34.2 CenterZ=0 NormalX=0 NormalY=0 NormalZ=1 AngleXU=0 Radius=3 StartAngle=1.5708 EndAngle=3.14159
    g16: ArcOfCircle CenterX=-10.2 CenterY=-34.2 CenterZ=0 NormalX=0 NormalY=0 NormalZ=1 AngleXU=0 Radius=3 StartAngle=3.14159 EndAngle=4.71239
    g17: ArcOfCircle CenterX=10.2 CenterY=-34.2 CenterZ=0 NormalX=0 NormalY=0 NormalZ=1 AngleXU=0 Radius=3 StartAngle=4.71239 EndAngle=6.28319
    g18: ArcOfCircle CenterX=10.2 CenterY=34.2 CenterZ=0 NormalX=0 NormalY=0 NormalZ=1 AngleXU=0 Radius=3 StartAngle=1e-16 EndAngle=1.5708
    g19: GeomPoint [constr] X=-13.2 Y=37.2 Z=0
    g20: GeomPoint [constr] X=13.2 Y=-37.2 Z=0
    g21: LineSegment [constr] StartX=-9.2 StartY=30 StartZ=0 EndX=-13.2 EndY=30 EndZ=0
    g22: LineSegment [constr] StartX=-6 StartY=33.2 StartZ=0 EndX=-6 EndY=37.2 EndZ=0
  constraints (53):
    c: Tangent(g0,g4) = -1.5708
    c: Tangent(g0,g5) = -1.5708
    c: Tangent(g1,g5) = -1.5708
    c: Tangent(g1,g6) = -1.5708
    c: Tangent(g2,g6) = -1.5708
    c: Tangent(g2,g7) = -1.5708
    c: Tangent(g3,g7) = -1.5708
    c: Tangent(g3,g4) = -1.5708
    c: Vertical(g0)
    c: Vertical(g2)
    c: Horizontal(g1)
    c: Horizontal(g3)
    c: Equal(g4,g5)
    c: Equal(g5,g6)
    c: Equal(g6,g7)
    c: PointOnObject(g8,g0)
    c: PointOnObject(g8,g3)
    c: PointOnObject(g9,g1)
    c: PointOnObject(g9,g2)
    c: Radius(g5) = 3.2
    c: Symmetric(g8,g9,g-1)
    c: DistanceX(g0,g2) = 18.4
    c: DistanceY(g1,g3) = 66.4
    c: Coincident(g-1,g10)
    c: Tangent(g11,g15) = -1.5708
    c: Tangent(g11,g16) = -1.5708
    c: Tangent(g12,g16) = -1.5708
    c: Tangent(g12,g17) = -1.5708
    c: Tangent(g13,g17) = -1.5708
    c: Tangent(g13,g18) = -1.5708
    c: Tangent(g14,g18) = -1.5708
    c: Tangent(g14,g15) = -1.5708
    c: Vertical(g11)
    c: Vertical(g13)
    c: Horizontal(g12)
    c: Horizontal(g14)
    c: Equal(g15,g16)
    c: Equal(g16,g17)
    c: Equal(g17,g18)
    c: PointOnObject(g19,g11)
    c: PointOnObject(g19,g14)
    c: PointOnObject(g20,g12)
    c: PointOnObject(g20,g13)
    c: Radius(g16) = 3
    c: Symmetric(g19,g20,g10)
    c: Coincident(g21,g0)
    c: PointOnObject(g21,g11)
    c: Horizontal(g21)
    c: DistanceX(g21,g21) = 4
    c: Coincident(g22,g3)
    c: PointOnObject(g22,g14)
    c: Vertical(g22)
    c: Equal(g21,g22)
FEATURE [PartDesign::Pad] Pad011  label="P-Radlagerfederung 1"
  Direction = (0,0,1)
  Length = 8
  Length2 = 10
  Profile = -> Sketch015
  ReferenceAxis = -> Sketch015 [N_Axis]
  Refine = true
  Suppressed = false
  Type = 0
FEATURE [Sketcher::SketchObject] Sketch016  label="Sk-Radlagerfeder Decke"
  ArcFitTolerance = 1e-06
  AttachmentSupport = -> [Pad011]
  ExternalGeometry = -> [Pad011]
  FullyConstrained = true
  MakeInternals = false
  MapMode = 5
  Placement = pos=(0,0,8) rot=(0,0,1;0rad)
  sketch-geometry (14):
    g0: LineSegment StartX=-13.2 StartY=34.2 StartZ=0 EndX=-13.2 EndY=-34.2 EndZ=0
    g1: LineSegment StartX=-10.2 StartY=-37.2 StartZ=0 EndX=10.2 EndY=-37.2 EndZ=0
    g2: LineSegment StartX=13.2 StartY=-34.2 StartZ=0 EndX=13.2 EndY=34.2 EndZ=0
    g3: LineSegment StartX=10.2 StartY=37.2 StartZ=0 EndX=-10.2 EndY=37.2 EndZ=0
    g4: ArcOfCircle CenterX=-10.2 CenterY=34.2 CenterZ=0 NormalX=0 NormalY=0 NormalZ=1 AngleXU=0 Radius=3 StartAngle=1.5708 EndAngle=3.14159
    g5: ArcOfCircle CenterX=-10.2 CenterY=-34.2 CenterZ=0 NormalX=0 NormalY=0 NormalZ=1 AngleXU=0 Radius=3 StartAngle=3.14159 EndAngle=4.71239
    g6: ArcOfCircle CenterX=10.2 CenterY=-34.2 CenterZ=0 NormalX=0 NormalY=0 NormalZ=1 AngleXU=0 Radius=3 StartAngle=4.71239 EndAngle=6.28319
    g7: ArcOfCircle CenterX=10.2 CenterY=34.2 CenterZ=0 NormalX=0 NormalY=0 NormalZ=1 AngleXU=0 Radius=3 StartAngle=4e-16 EndAngle=1.5708
    g8: GeomPoint [constr] X=-13.2 Y=37.2 Z=0
    g9: GeomPoint [constr] X=13.2 Y=-37.2 Z=0
    g10: LineSegment [constr] StartX=0 StartY=33.2 StartZ=0 EndX=0 EndY=16.5 EndZ=0
    g11: LineSegment [constr] StartX=0 StartY=16.5 StartZ=0 EndX=0 EndY=-16.5 EndZ=0
    g12: Circle CenterX=0 CenterY=16.5 CenterZ=0 NormalX=0 NormalY=0 NormalZ=1 AngleXU=0 Radius=3.2
    g13: Circle CenterX=0 CenterY=-16.5 CenterZ=0 NormalX=0 NormalY=0 NormalZ=1 AngleXU=0 Radius=3.2
  constraints (32):
    c: Tangent(g0,g4) = -1.5708
    c: Tangent(g0,g5) = -1.5708
    c: Tangent(g1,g5) = -1.5708
    c: Tangent(g1,g6) = -1.5708
    c: Tangent(g2,g6) = -1.5708
    c: Tangent(g2,g7) = -1.5708
    c: Tangent(g3,g7) = -1.5708
    c: Tangent(g3,g4) = -1.5708
    c: Vertical(g0)
    c: Vertical(g2)
    c: Horizontal(g1)
    c: Horizontal(g3)
    c: Equal(g4,g5)
    c: Equal(g5,g6)
    c: Equal(g6,g7)
    c: PointOnObject(g8,g0)
    c: PointOnObject(g8,g3)
    c: PointOnObject(g9,g1)
    c: PointOnObject(g9,g2)
    c: Equal(g4,g-3)
    c: Coincident(g3,g-3)
    c: Coincident(g1,g-4)
    c: Distance(g10) = 16.7
    c: PointOnObject(g10,g-5)
    c: Vertical(g10)
    c: PointOnObject(g10,g-2)
    c: Coincident(g11,g10)
    c: Symmetric(g11,g10,g-1)
    c: Diameter(g12) = 6.4
    c: Coincident(g12,g10)
    c: Coincident(g13,g11)
    c: Equal(g12,g13)
FEATURE [PartDesign::Pad] Pad012  label="P-Radlagerfederung 2"
  BaseFeature = -> Pad011
  Direction = (0,0,1)
  Length = 4
  Length2 = 10
  Profile = -> Sketch016
  ReferenceAxis = -> Sketch016 [N_Axis]
  Refine = true
  Suppressed = false
  Type = 0
FEATURE [Sketcher::SketchObject] Sketch017  label="Sk-Radlagerfeder Lager"
  ArcFitTolerance = 1e-06
  AttachmentSupport = -> [Pad012]
  ExternalGeometry = -> [Pad012]
  FullyConstrained = true
  MakeInternals = false
  MapMode = 5
  Placement = pos=(0,0,12) rot=(0,0,1;0rad)
  sketch-geometry (12):
    g0: Circle [constr] CenterX=0 CenterY=16.5 CenterZ=0 NormalX=0 NormalY=0 NormalZ=1 AngleXU=0 Radius=7
    g1: Circle [constr] CenterX=0 CenterY=-16.5 CenterZ=0 NormalX=0 NormalY=0 NormalZ=1 AngleXU=0 Radius=7
    g2: LineSegment StartX=-13.2 StartY=7 StartZ=0 EndX=-13.2 EndY=-7 EndZ=0
    g3: LineSegment StartX=-11.2 StartY=-9 StartZ=0 EndX=11.2 EndY=-9 EndZ=0
    g4: LineSegment StartX=13.2 StartY=-7 StartZ=0 EndX=13.2 EndY=7 EndZ=0
    g5: LineSegment StartX=11.2 StartY=9 StartZ=0 EndX=-11.2 EndY=9 EndZ=0
    g6: ArcOfCircle CenterX=-11.2 CenterY=7 CenterZ=0 NormalX=0 NormalY=0 NormalZ=1 AngleXU=0 Radius=2 StartAngle=1.5708 EndAngle=3.14159
    g7: ArcOfCircle CenterX=-11.2 CenterY=-7 CenterZ=0 NormalX=0 NormalY=0 NormalZ=1 AngleXU=0 Radius=2 StartAngle=3.14159 EndAngle=4.71239
    g8: ArcOfCircle CenterX=11.2 CenterY=-7 CenterZ=0 NormalX=0 NormalY=0 NormalZ=1 AngleXU=0 Radius=2 StartAngle=4.71239 EndAngle=6.28319
    g9: ArcOfCircle CenterX=11.2 CenterY=7 CenterZ=0 NormalX=0 NormalY=0 NormalZ=1 AngleXU=0 Radius=2 StartAngle=2e-16 EndAngle=1.5708
    g10: GeomPoint [constr] X=-13.2 Y=9 Z=0
    g11: GeomPoint [constr] X=13.2 Y=-9 Z=0
  constraints (27):
    c: Diameter(g0) = 14
    c: Coincident(g0,g-5)
    c: Coincident(g1,g-6)
    c: Equal(g0,g1)
    c: Tangent(g2,g6) = -1.5708
    c: Tangent(g2,g7) = -1.5708
    c: Tangent(g3,g7) = -1.5708
    c: Tangent(g3,g8) = -1.5708
    c: Tangent(g4,g8) = -1.5708
    c: Tangent(g4,g9) = -1.5708
    c: Tangent(g5,g9) = -1.5708
    c: Tangent(g5,g6) = -1.5708
    c: Vertical(g2)
    c: Vertical(g4)
    c: Horizontal(g3)
    c: Horizontal(g5)
    c: Equal(g7,g8)
    c: Equal(g8,g9)
    c: PointOnObject(g10,g2)
    c: PointOnObject(g10,g5)
    c: PointOnObject(g11,g3)
    c: PointOnObject(g11,g4)
    c: Radius(g7) = 2
    c: PointOnObject(g10,g-3)
    c: PointOnObject(g11,g-4)
    c: DistanceY(g3,g5) = 18
    c: Symmetric(g5,g3,g-1)
FEATURE [PartDesign::Pad] Pad013  label="P-Radlagerfederung 3"
  BaseFeature = -> Pad012
  Direction = (0,0,1)
  Length = 14
  Length2 = 10
  Profile = -> Sketch017
  ReferenceAxis = -> Sketch017 [N_Axis]
  Refine = true
  Suppressed = false
  Type = 0
FEATURE [PartDesign::Fillet] Fillet  label="P-Radlagerfederung 4"
  Base = -> Pad013 [Edge72]
  BaseFeature = -> Pad013
  Radius = 2
  Refine = true
  SupportTransform = false
  Suppressed = false
  UseAllEdges = false
FEATURE [Sketcher::SketchObject] Sketch018  label="Sk-Radlagerfeder Wellenbohrung"
  ArcFitTolerance = 1e-06
  AttachmentSupport = -> [Fillet]
  FullyConstrained = true
  MakeInternals = false
  MapMode = 5
  Placement = pos=(-13.2,0,0) rot=(0.57735,-0.57735,-0.57735;2.0944rad)
  sketch-geometry (2):
    g0: Circle CenterX=0 CenterY=17 CenterZ=0 NormalX=0 NormalY=0 NormalZ=1 AngleXU=0 Radius=4.2
    g1: LineSegment [constr] StartX=0 StartY=17 StartZ=0 EndX=0 EndY=0 EndZ=0
  constraints (5):
    c: Diameter(g0) = 8.4
    c: PointOnObject(g0,g-2)
    c: Coincident(g1,g0)
    c: Coincident(g1,g-1)
    c: DistanceY(g1,g1) = 17
FEATURE [PartDesign::Pocket] Pocket
  BaseFeature = -> Fillet
  Direction = (1,0,0)
  Length = 5
  Length2 = 5
  Profile = -> Sketch018
  ReferenceAxis = -> Sketch018 [N_Axis]
  Refine = true
  Suppressed = false
  Type = 1
FEATURE [PartDesign::Body] Body012  label="B-Radlagerfederung"
  AllowCompound = false
  Group = -> [Sketch015,Pad011,Sketch016,Pad012,Sketch017,Pad013,Fillet,Sketch018,Pocket]
  Origin = -> Origin011
  Tip = -> Pocket
FEATURE [Part::Feature] Body014  label="S-Radlagerfederung links"
  Placement = pos=(0,0,3) rot=(0,0,1;0rad)
  shape: bbox 26.4 x 74.4 x 26 mm, 38 faces (baked)
FEATURE [Mesh::Feature] Mesh002  label="M-Radlagerfederung"
FEATURE [Part::Feature] Body015  label="S-Radlagerbasis links"
  shape: bbox 18 x 66 x 8.2 mm, 35 faces (baked)
FEATURE [Mesh::Feature] Mesh003  label="M-Radlagerbasis"
FEATURE [App::FeaturePython] GroundedJoint  # Assembly grounded joint (typed FeaturePython)
  ObjectToGround = -> Body009
FEATURE [Assembly::JointGroup] Joints
  Group = -> [GroundedJoint]
FEATURE [Part::FeaturePython] Screw  label="M6x50-Schraube 1 links"  # WARN: FeaturePython — macro-defined, semantics opaque (R4)
  Diameter = 8
  Invert = false
  LeftHanded = false
  Length = 4
  LengthCustom = 50
  MatchOuter = false
  OffsetAngle = 0
  Placement = pos=(-5e-16,-16.5,4) rot=(0,1,0;3.14159rad)
  Thread = true
  Type = 65
FEATURE [Part::FeaturePython] Screw001  label="M6x50-Schraube 2 links"  # WARN: FeaturePython — macro-defined, semantics opaque (R4)
  Diameter = 8
  Invert = false
  LeftHanded = false
  Length = 4
  LengthCustom = 50
  MatchOuter = false
  OffsetAngle = 0
  Placement = pos=(-5e-16,16.5,4) rot=(0,1,0;3.14159rad)
  Thread = true
  Type = 65
FEATURE [Part::FeaturePython] Washer  label="M6-Scheibe 1 links"  # WARN: FeaturePython — macro-defined, semantics opaque (R4)
  Diameter = 7
  Invert = true
  MatchOuter = false
  OffsetAngle = 0
  Placement = pos=(0,16.5,45.35) rot=(0,0,1;0rad)
  Type = 8
FEATURE [Part::FeaturePython] Washer001  label="M6-Scheibe 2 links"  # WARN: FeaturePython — macro-defined, semantics opaque (R4)
  Diameter = 7
  Invert = true
  MatchOuter = false
  OffsetAngle = 0
  Placement = pos=(0,-16.5,45.35) rot=(0,0,1;0rad)
  Type = 8
FEATURE [Part::FeaturePython] Nut  label="M6-Mutter 1 links"  # WARN: FeaturePython — macro-defined, semantics opaque (R4)
  Diameter = 2
  Invert = false
  LeftHanded = false
  MatchOuter = false
  OffsetAngle = 0
  Placement = pos=(0,-16.5,47) rot=(0,0,1;0rad)
  Thread = false
  Type = 40
FEATURE [Part::FeaturePython] Nut001  label="M6-Mutter 2 links"  # WARN: FeaturePython — macro-defined, semantics opaque (R4)
  Diameter = 2
  Invert = false
  LeftHanded = false
  MatchOuter = false
  OffsetAngle = 0
  Placement = pos=(0,16.5,47) rot=(0,0,1;0rad)
  Thread = false
  Type = 40
FEATURE [App::DocumentObjectGroup] Measurements
FEATURE [Sketcher::SketchObject] Sketch019  label="Sk-Feder 9x35 Profil"
  ArcFitTolerance = 1e-06
  AttachmentSupport = -> [XZ_Plane014]
  FullyConstrained = true
  MakeInternals = false
  MapMode = 5
  Placement = pos=(0,0,0) rot=(1,0,0;1.5708rad)
  sketch-geometry (1):
    g0: Circle CenterX=5 CenterY=0 CenterZ=0 NormalX=0 NormalY=0 NormalZ=1 AngleXU=0 Radius=0.5
  constraints (3):
    c: Diameter(g0) = 1
    c: PointOnObject(g0,g-1)
    c: DistanceX(g-1,g0) = 5
FEATURE [PartDesign::AdditiveHelix] AdditiveHelix  label="P-Feder 9x35"
  Angle = 0
  Axis = (0,2e-16,1)
  Base = (0,0,0)
  Growth = 0
  HasBeenEdited = true
  Height = 31.25
  LeftHanded = false
  Mode = 0
  Outside = false
  Pitch = 3
  Placement = pos=(0,0,0) rot=(1,0,0;1.5708rad)
  Profile = -> Sketch019
  ReferenceAxis = -> Sketch019 [V_Axis]
  Refine = true
  Suppressed = false
  Tolerance = 0.1
  Turns = 10.4167
FEATURE [PartDesign::Body] Body018  label="B-Feder 9x35"
  AllowCompound = false
  Group = -> [Sketch019,AdditiveHelix]
  Origin = -> Origin014
  Tip = -> AdditiveHelix
FEATURE [Part::Feature] Body020  label="S-Feder 9x35 1 links"
  Placement = pos=(0,-16.5,15) rot=(0,0,1;0rad)
  shape: bbox 14.35 x 16.09 x 33.15 mm, 13 faces (baked)
FEATURE [Part::Feature] Body021  label="S-Feder 9x35 2 links"
  Placement = pos=(0,16.5,15) rot=(0,0,1;0rad)
  shape: bbox 14.35 x 16.09 x 33.15 mm, 13 faces (baked)
FEATURE [Part::FeaturePython] Washer002  label="M6-Scheibe"  # WARN: FeaturePython — macro-defined, semantics opaque (R4)
  Diameter = 7
  Invert = true
  MatchOuter = false
  OffsetAngle = 0
  Placement = pos=(0,16.5,15) rot=(0,0,1;0rad)
  Type = 8
FEATURE [Part::FeaturePython] Washer003  label="M6-Scheibe001"  # WARN: FeaturePython — macro-defined, semantics opaque (R4)
  Diameter = 7
  Invert = true
  MatchOuter = false
  OffsetAngle = 0
  Placement = pos=(0,-16.5,15) rot=(0,0,1;0rad)
  Type = 8
FEATURE [Part::Feature] Body022  label="S-Radlagerfederung rechts"
  Placement = pos=(0,0,3) rot=(0,0,1;0rad)
  shape: bbox 26.4 x 74.4 x 26 mm, 38 faces (baked)
FEATURE [Part::Feature] Body023  label="S-Radlagerbasis rechts"
  shape: bbox 18 x 66 x 8.2 mm, 35 faces (baked)
FEATURE [Part::Feature] Body024  label="S-Feder 9x35 1 rechts"
  Placement = pos=(0,-16.5,15) rot=(0,0,1;0rad)
  shape: bbox 14.35 x 16.09 x 33.15 mm, 13 faces (baked)
FEATURE [Part::Feature] Body025  label="S-Feder 9x35 2 rechts"
  Placement = pos=(0,16.5,15) rot=(0,0,1;0rad)
  shape: bbox 14.35 x 16.09 x 33.15 mm, 13 faces (baked)
FEATURE [Part::FeaturePython] Nut002  label="M6-Mutter 1 rechts"  # WARN: FeaturePython — macro-defined, semantics opaque (R4)
  Diameter = 2
  Invert = false
  LeftHanded = false
  MatchOuter = false
  OffsetAngle = 0
  Placement = pos=(0,-16.5,47) rot=(0,0,1;0rad)
  Thread = false
  Type = 40
FEATURE [Part::FeaturePython] Nut003  label="M6-Mutter 2 rechts"  # WARN: FeaturePython — macro-defined, semantics opaque (R4)
  Diameter = 2
  Invert = false
  LeftHanded = false
  MatchOuter = false
  OffsetAngle = 0
  Placement = pos=(0,16.5,47) rot=(0,0,1;0rad)
  Thread = false
  Type = 40
FEATURE [Part::FeaturePython] Screw002  label="M6x50-Schraube 1 rechts"  # WARN: FeaturePython — macro-defined, semantics opaque (R4)
  Diameter = 8
  Invert = false
  LeftHanded = false
  Length = 4
  LengthCustom = 50
  MatchOuter = false
  OffsetAngle = 0
  Placement = pos=(-5e-16,-16.5,4) rot=(0,1,0;3.14159rad)
  Thread = true
  Type = 65
FEATURE [Part::FeaturePython] Screw003  label="M6x50-Schraube 2 rechts"  # WARN: FeaturePython — macro-defined, semantics opaque (R4)
  Diameter = 8
  Invert = false
  LeftHanded = false
  Length = 4
  LengthCustom = 50
  MatchOuter = false
  OffsetAngle = 0
  Placement = pos=(-5e-16,16.5,4) rot=(0,1,0;3.14159rad)
  Thread = true
  Type = 65
FEATURE [Part::FeaturePython] Washer004  label="M6-Scheibe 1 rechts"  # WARN: FeaturePython — macro-defined, semantics opaque (R4)
  Diameter = 7
  Invert = true
  MatchOuter = false
  OffsetAngle = 0
  Placement = pos=(0,16.5,45.35) rot=(0,0,1;0rad)
  Type = 8
FEATURE [Part::FeaturePython] Washer005  label="M6-Scheibe 2 rechts"  # WARN: FeaturePython — macro-defined, semantics opaque (R4)
  Diameter = 7
  Invert = true
  MatchOuter = false
  OffsetAngle = 0
  Placement = pos=(0,-16.5,45.35) rot=(0,0,1;0rad)
  Type = 8
FEATURE [Part::FeaturePython] Washer006  label="M6-Scheibe 3 rechts"  # WARN: FeaturePython — macro-defined, semantics opaque (R4)
  Diameter = 7
  Invert = true
  MatchOuter = false
  OffsetAngle = 0
  Placement = pos=(0,16.5,15) rot=(0,0,1;0rad)
  Type = 8
FEATURE [Part::FeaturePython] Washer007  label="M6-Scheibe 4 rechts"  # WARN: FeaturePython — macro-defined, semantics opaque (R4)
  Diameter = 7
  Invert = true
  MatchOuter = false
  OffsetAngle = 0
  Placement = pos=(0,-16.5,15) rot=(0,0,1;0rad)
  Type = 8
FEATURE [Part::FeaturePython] Screw005  label="#8x20-Schraube"  # WARN: FeaturePython — macro-defined, semantics opaque (R4)
  Diameter = 9
  Invert = false
  LeftHanded = false
  Length = 13
  LengthCustom = 20
  MatchOuter = false
  OffsetAngle = 0
  Placement = pos=(0,0,6) rot=(0,0,1;0rad)
  Thread = false
  Type = 15
FEATURE [Part::FeaturePython] Screw006  label="#8x20-Schraube005"  # WARN: FeaturePython — macro-defined, semantics opaque (R4)
  Diameter = 9
  Invert = false
  LeftHanded = false
  Length = 13
  LengthCustom = 20
  MatchOuter = false
  OffsetAngle = 0
  Placement = pos=(0,-27.6,6) rot=(0,0,1;0rad)
  Thread = false
  Type = 15
FEATURE [Part::FeaturePython] Screw007  label="#8x20-Schraube006"  # WARN: FeaturePython — macro-defined, semantics opaque (R4)
  Diameter = 9
  Invert = false
  LeftHanded = false
  Length = 13
  LengthCustom = 20
  MatchOuter = false
  OffsetAngle = 0
  Placement = pos=(0,27.6,6) rot=(0,0,1;0rad)
  Thread = false
  Type = 15
FEATURE [App::Part] Part003  label="Radlager links"
  Group = -> [Body015,Body014,Screw,Screw001,Washer,Washer001,Nut,Nut001,Body020,Body021,Washer002,Washer003,Screw005,Screw006,Screw007]
  Origin = -> Origin012
  Placement = pos=(-34,0,0) rot=(0,0,1;0rad)
FEATURE [Part::FeaturePython] Screw008  label="#8x20-Schraube010"  # WARN: FeaturePython — macro-defined, semantics opaque (R4)
  Diameter = 9
  Invert = false
  LeftHanded = false
  Length = 13
  LengthCustom = 20
  MatchOuter = false
  OffsetAngle = 0
  Placement = pos=(0,0,6) rot=(0,0,1;0rad)
  Thread = false
  Type = 15
FEATURE [Part::FeaturePython] Screw009  label="#8x20-Schraube011"  # WARN: FeaturePython — macro-defined, semantics opaque (R4)
  Diameter = 9
  Invert = false
  LeftHanded = false
  Length = 13
  LengthCustom = 20
  MatchOuter = false
  OffsetAngle = 0
  Placement = pos=(0,-27.6,6) rot=(0,0,1;0rad)
  Thread = false
  Type = 15
FEATURE [Part::FeaturePython] Screw010  label="#8x20-Schraube012"  # WARN: FeaturePython — macro-defined, semantics opaque (R4)
  Diameter = 9
  Invert = false
  LeftHanded = false
  Length = 13
  LengthCustom = 20
  MatchOuter = false
  OffsetAngle = 0
  Placement = pos=(0,27.6,6) rot=(0,0,1;0rad)
  Thread = false
  Type = 15
FEATURE [App::Part] Part004  label="Radlager rechts"
  Group = -> [Body023,Body022,Screw002,Screw003,Washer004,Washer005,Nut002,Nut003,Body024,Body025,Washer006,Washer007,Screw008,Screw009,Screw010]
  Origin = -> Origin015
  Placement = pos=(34,0,0) rot=(0,0,1;0rad)
FEATURE [Part::FeaturePython] Screw011  label="M8x120-Schraube"  # WARN: FeaturePython — macro-defined, semantics opaque (R4)
  Diameter = 3
  Invert = false
  LeftHanded = false
  Length = 5
  LengthCustom = 120
  MatchOuter = false
  OffsetAngle = 0
  Placement = pos=(-49,0,23) rot=(0,1,0;4.71239rad)
  Thread = false
  Type = 67
FEATURE [Part::FeaturePython] Washer008  label="M8-Scheibe"  # WARN: FeaturePython — macro-defined, semantics opaque (R4)
  Diameter = 8
  Invert = false
  MatchOuter = false
  OffsetAngle = 0
  Placement = pos=(-49,0,23) rot=(0,1,0;1.5708rad)
  Type = 8
FEATURE [Part::FeaturePython] Washer009  label="M8-Scheibe001"  # WARN: FeaturePython — macro-defined, semantics opaque (R4)
  Diameter = 8
  Invert = false
  MatchOuter = false
  OffsetAngle = 0
  Placement = pos=(49,0,23) rot=(0,1,0;4.71239rad)
  Type = 8
FEATURE [Part::FeaturePython] Nut004  label="M8-Mutter"  # WARN: FeaturePython — macro-defined, semantics opaque (R4)
  Diameter = 3
  Invert = false
  LeftHanded = false
  MatchOuter = false
  OffsetAngle = 0
  Placement = pos=(49,0,23) rot=(0,-1,0;4.71239rad)
  Thread = false
  Type = 40
FEATURE [App::Part] Part001  label="Rad"
  Group = -> [Body002,Part003,Part004,Screw011,Washer008,Washer009,Nut004]
  Origin = -> Origin007
FEATURE [Sketcher::SketchObject] Sketch020  label="Sk-Stepperwippe - Bodenplatte"
  ArcFitTolerance = 1e-06
  AttachmentSupport = -> [XY_Plane016]
  FullyConstrained = false
  MakeInternals = false
  MapMode = 5
  sketch-geometry (50):
    g0: LineSegment StartX=-21 StartY=24 StartZ=0 EndX=-31 EndY=24 EndZ=0
    g1: LineSegment StartX=71 StartY=0 StartZ=0 EndX=71 EndY=90 EndZ=0
    g2: LineSegment StartX=71 StartY=90 StartZ=0 EndX=21 EndY=90 EndZ=0
    g3: LineSegment StartX=-31 StartY=0 StartZ=0 EndX=71 EndY=0 EndZ=0
    g4: LineSegment StartX=17 StartY=20 StartZ=0 EndX=-17 EndY=20 EndZ=0
    g5: LineSegment StartX=21 StartY=90 StartZ=0 EndX=21 EndY=24 EndZ=0
    g6: LineSegment StartX=31 StartY=38 StartZ=0 EndX=31 EndY=24 EndZ=0
    g7: LineSegment StartX=35 StartY=20 StartZ=0 EndX=57 EndY=20 EndZ=0
    g8: LineSegment StartX=61 StartY=24 StartZ=0 EndX=61 EndY=38 EndZ=0
    g9: LineSegment StartX=57 StartY=42 StartZ=0 EndX=35 EndY=42 EndZ=0
    g10: LineSegment [constr] StartX=21 StartY=20 StartZ=0 EndX=31 EndY=20 EndZ=0
    g11: ArcOfCircle CenterX=-17 CenterY=24 CenterZ=0 NormalX=0 NormalY=0 NormalZ=1 AngleXU=0 Radius=4 StartAngle=3.14159 EndAngle=4.71239
    g12: GeomPoint [constr] X=-21 Y=20 Z=0
    g13: ArcOfCircle CenterX=17 CenterY=24 CenterZ=0 NormalX=0 NormalY=0 NormalZ=1 AngleXU=0 Radius=4 StartAngle=4.71239 EndAngle=6.28319
    g14: GeomPoint [constr] X=21 Y=20 Z=0
    g15: ArcOfCircle CenterX=35 CenterY=24 CenterZ=0 NormalX=0 NormalY=0 NormalZ=1 AngleXU=0 Radius=4 StartAngle=3.14159 EndAngle=4.71239
    g16: GeomPoint [constr] X=31 Y=20 Z=0
    g17: ArcOfCircle CenterX=57 CenterY=24 CenterZ=0 NormalX=0 NormalY=0 NormalZ=1 AngleXU=0 Radius=4 StartAngle=4.71239 EndAngle=6.28319
    g18: GeomPoint [constr] X=61 Y=20 Z=0
    g19: ArcOfCircle CenterX=57 CenterY=38 CenterZ=0 NormalX=0 NormalY=0 NormalZ=1 AngleXU=0 Radius=4 StartAngle=3e-16 EndAngle=1.5708
    g20: GeomPoint [constr] X=61 Y=42 Z=0
    g21: ArcOfCircle CenterX=35 CenterY=38 CenterZ=0 NormalX=0 NormalY=0 NormalZ=1 AngleXU=0 Radius=4 StartAngle=1.5708 EndAngle=3.14159
    g22: GeomPoint [constr] X=31 Y=42 Z=0
    g23: LineSegment [constr] StartX=31 StartY=38 StartZ=0 EndX=21 EndY=38 EndZ=0
    g24: LineSegment [constr] StartX=61 StartY=38 StartZ=0 EndX=71 EndY=38 EndZ=0
    g25: LineSegment StartX=26 StartY=76 StartZ=0 EndX=26 EndY=56 EndZ=0
    g26: LineSegment StartX=30 StartY=52 StartZ=0 EndX=57 EndY=52 EndZ=0
    g27: LineSegment StartX=61 StartY=56 StartZ=0 EndX=61 EndY=76 EndZ=0
    g28: LineSegment StartX=57 StartY=80 StartZ=0 EndX=30 EndY=80 EndZ=0
    g29: ArcOfCircle CenterX=30 CenterY=76 CenterZ=0 NormalX=0 NormalY=0 NormalZ=1 AngleXU=0 Radius=4 StartAngle=1.5708 EndAngle=3.14159
    g30: ArcOfCircle CenterX=30 CenterY=56 CenterZ=0 NormalX=0 NormalY=0 NormalZ=1 AngleXU=0 Radius=4 StartAngle=3.14159 EndAngle=4.71239
    g31: ArcOfCircle CenterX=57 CenterY=56 CenterZ=0 NormalX=0 NormalY=0 NormalZ=1 AngleXU=0 Radius=4 StartAngle=4.71239 EndAngle=6.28319
    g32: ArcOfCircle CenterX=57 CenterY=76 CenterZ=0 NormalX=0 NormalY=0 NormalZ=1 AngleXU=0 Radius=4 StartAngle=1.2e-15 EndAngle=1.5708
    g33: GeomPoint [constr] X=26 Y=80 Z=0
    g34: GeomPoint [constr] X=61 Y=52 Z=0
    g35: LineSegment [constr] StartX=57 StartY=80 StartZ=0 EndX=57 EndY=90 EndZ=0
    g36: LineSegment [constr] StartX=57 StartY=52 StartZ=0 EndX=57 EndY=42 EndZ=0
    g37: LineSegment StartX=-31 StartY=24 StartZ=0 EndX=-31 EndY=0 EndZ=0
    g38: LineSegment [constr] StartX=57 StartY=20 StartZ=0 EndX=57 EndY=0 EndZ=0
    g39: LineSegment [constr] StartX=-21 StartY=24 StartZ=0 EndX=0 EndY=24 EndZ=0
    g40: LineSegment [constr] StartX=0 StartY=24 StartZ=0 EndX=21 EndY=24 EndZ=0
    g41: LineSegment [constr] StartX=26 StartY=56 StartZ=0 EndX=21 EndY=56 EndZ=0
    g42: LineSegment [constr] StartX=23 StartY=88 StartZ=0 EndX=23 EndY=44 EndZ=0
    g43: LineSegment [constr] StartX=23 StartY=44 StartZ=0 EndX=71 EndY=44 EndZ=0
    g44: LineSegment [constr] StartX=71 StartY=44 StartZ=0 EndX=71 EndY=88 EndZ=0
    g45: LineSegment [constr] StartX=71 StartY=88 StartZ=0 EndX=23 EndY=88 EndZ=0
    g46: LineSegment [constr] StartX=23 StartY=88 StartZ=0 EndX=21 EndY=88 EndZ=0
    g47: LineSegment [constr] StartX=23 StartY=88 StartZ=0 EndX=23 EndY=90 EndZ=0
    g48: LineSegment [constr] StartX=23 StartY=44 StartZ=0 EndX=23 EndY=42 EndZ=0
    g49: LineSegment [constr] StartX=21 StartY=42 StartZ=0 EndX=71 EndY=42 EndZ=0
  constraints (132):
    c: Horizontal(g0)
    c: Coincident(g1,g2)
    c: Coincident(g2,g5)
    c: Vertical(g1)
    c: Horizontal(g2)
    c: PointOnObject(g1,g-1)
    c: Coincident(g37,g3)
    c: Horizontal(g3)
    c: Horizontal(g4)
    c: Vertical(g5)
    c: DistanceX(g0,g0) = 10
    c: DistanceX(g2,g2) = 50
    c: DistanceY(g1,g1) = 90
    c: Coincident(g3,g1)
    c: DistanceY(g14,g5) = 70
    c: Vertical(g6)
    c: Vertical(g8)
    c: Horizontal(g7)
    c: Horizontal(g9)
    c: Coincident(g10,g14)
    c: Coincident(g10,g16)
    c: Horizontal(g10)
    c: PointOnObject(g12,g4)
    c: Tangent(g4,g11) = 1.5708
    c: PointOnObject(g14,g4)
    c: PointOnObject(g14,g5)
    c: Tangent(g4,g13) = 1.5708
    c: Tangent(g5,g13) = 1.5708
    c: PointOnObject(g16,g6)
    c: PointOnObject(g16,g7)
    c: Tangent(g6,g15) = -1.5708
    c: Tangent(g7,g15) = -1.5708
    c: PointOnObject(g18,g7)
    c: PointOnObject(g18,g8)
    c: Tangent(g7,g17) = -1.5708
    c: Tangent(g8,g17) = -1.5708
    c: PointOnObject(g20,g9)
    c: PointOnObject(g20,g8)
    c: Tangent(g9,g19) = -1.5708
    c: Tangent(g8,g19) = -1.5708
    c: PointOnObject(g22,g9)
    c: PointOnObject(g22,g6)
    c: Tangent(g9,g21) = -1.5708
    c: Tangent(g6,g21) = -1.5708
    c: Equal(g11,g13)
    c: Equal(g13,g21)
    c: Equal(g21,g19)
    c: Equal(g19,g17)
    c: Equal(g17,g15)
    c: Radius(g21) = 4
    c: Coincident(g23,g6)
    c: PointOnObject(g23,g5)
    c: Horizontal(g23)
    c: Coincident(g24,g8)
    c: PointOnObject(g24,g1)
    c: Horizontal(g24)
    c: Equal(g24,g23)
    c: DistanceX(g23,g23) = 10
    c: Tangent(g25,g29) = -1.5708
    c: Tangent(g25,g30) = -1.5708
    c: Tangent(g26,g30) = -1.5708
    c: Tangent(g26,g31) = -1.5708
    c: Tangent(g27,g31) = -1.5708
    c: Tangent(g27,g32) = -1.5708
    c: Tangent(g28,g32) = -1.5708
    c: Tangent(g28,g29) = -1.5708
    c: Vertical(g25)
    c: Vertical(g27)
    c: Horizontal(g26)
    c: Horizontal(g28)
    c: Equal(g29,g30)
    c: Equal(g30,g31)
    c: Equal(g31,g32)
    c: PointOnObject(g33,g25)
    c: PointOnObject(g33,g28)
    c: PointOnObject(g34,g26)
    c: PointOnObject(g34,g27)
    c: Equal(g29,g15)
    c: Coincident(g35,g28)
    c: PointOnObject(g35,g2)
    c: Vertical(g35)
    c: Coincident(g36,g26)
    c: Coincident(g36,g9)
    c: Vertical(g36)
    c: Equal(g36,g35)
    c: Equal(g36,g24)
    c: Vertical(g37)
    c: Coincident(g37,g0)
    c: Coincident(g38,g7)
    c: PointOnObject(g38,g3)
    c: Vertical(g38)
    c: DistanceY(g38,g38) = 20
    c: PointOnObject(g40,g5)
    c: Coincident(g39,g40)
    c: Horizontal(g39)
    c: Horizontal(g40)
    c: PointOnObject(g39,g-2)
    c: Equal(g39,g40)
    c: DistanceX(g0,g40) = 42
    c: Coincident(g41,g25)
    c: PointOnObject(g41,g5)
    c: Horizontal(g41)
    c: DistanceX(g41,g41) = 5
    c: Coincident(g42,g43)
    c: Coincident(g43,g44)
    c: Coincident(g44,g45)
    c: Coincident(g45,g42)
    c: Vertical(g42)
    c: Vertical(g44)
    c: Horizontal(g43)
    c: Horizontal(g45)
    c: DistanceY(g44,g44) = 44
    c: DistanceX(g45,g45) = 48
    c: Coincident(g46,g42)
    c: PointOnObject(g46,g5)
    c: Horizontal(g46)
    c: Coincident(g47,g42)
    c: PointOnObject(g47,g2)
    c: Vertical(g47)
    c: Equal(g46,g47)
    c: DistanceX(g46,g46) = 2
    c: Coincident(g48,g42)
    c: Vertical(g48)
    c: PointOnObject(g49,g5)
    c: Horizontal(g49)
    c: PointOnObject(g49,g1)
    c: PointOnObject(g48,g49)
    c: Equal(g48,g46)
    c: PointOnObject(g9,g49)
    c: Coincident(g0,g11)
    c: Coincident(g39,g0)
    c: Perpendicular(g11,g0)
FEATURE [PartDesign::Pad] Pad014  label="P-Stepperwippe - Bodenplatte"
  Direction = (0,0,1)
  Length = 3
  Length2 = 10
  Profile = -> Sketch020
  ReferenceAxis = -> Sketch020 [N_Axis]
  Refine = true
  Suppressed = false
  Type = 0
FEATURE [Sketcher::SketchObject] Sketch021  label="Sk-Stepperwippe - Stepperfront"
  ArcFitTolerance = 1e-06
  AttachmentSupport = -> [Pad014]
  ExternalGeometry = -> [Pad014]
  FullyConstrained = true
  MakeInternals = false
  MapMode = 5
  Placement = pos=(21,0,0) rot=(0.57735,-0.57735,-0.57735;2.0944rad)
  sketch-geometry (8):
    g0: LineSegment StartX=-90 StartY=3 StartZ=0 EndX=-41 EndY=3 EndZ=0
    g1: LineSegment StartX=-41 StartY=3 StartZ=0 EndX=-41 EndY=43 EndZ=0
    g2: LineSegment StartX=-44 StartY=46 StartZ=0 EndX=-87 EndY=46 EndZ=0
    g3: LineSegment StartX=-90 StartY=43 StartZ=0 EndX=-90 EndY=3 EndZ=0
    g4: ArcOfCircle CenterX=-87 CenterY=43 CenterZ=0 NormalX=0 NormalY=0 NormalZ=1 AngleXU=0 Radius=3 StartAngle=1.5708 EndAngle=3.14159
    g5: GeomPoint [constr] X=-90 Y=46 Z=0
    g6: ArcOfCircle CenterX=-44 CenterY=43 CenterZ=0 NormalX=0 NormalY=0 NormalZ=1 AngleXU=0 Radius=3 StartAngle=-2.86544e-11 EndAngle=1.5708
    g7: GeomPoint [constr] X=-41 Y=46 Z=0
  constraints (19):
    c: Coincident(g0,g1)
    c: Coincident(g3,g0)
    c: Horizontal(g0)
    c: Horizontal(g2)
    c: Vertical(g1)
    c: Vertical(g3)
    c: Coincident(g0,g-3)
    c: DistanceX(g5,g7) = 49
    c: PointOnObject(g5,g3)
    c: PointOnObject(g5,g2)
    c: Tangent(g3,g4) = -1.5708
    c: Tangent(g2,g4) = -1.5708
    c: PointOnObject(g7,g2)
    c: PointOnObject(g7,g1)
    c: Tangent(g2,g6) = -1.5708
    c: Tangent(g1,g6) = -1.5708
    c: Radius(g4) = 3
    c: DistanceY(g0,g2) = 43
    c: Equal(g4,g6)
FEATURE [PartDesign::Pad] Pad015  label="P-Stepperwippe - Front"
  BaseFeature = -> Pad014
  Direction = (-1,0,0)
  Length = 2
  Length2 = 10
  Profile = -> Sketch021
  ReferenceAxis = -> Sketch021 [N_Axis]
  Refine = true
  Reversed = true
  Suppressed = false
  Type = 0
FEATURE [Sketcher::SketchObject] Sketch022  label="Sk-Stepperwippe - Frontstrebe links"
  ArcFitTolerance = 1e-06
  AttachmentSupport = -> [Pad015]
  ExternalGeometry = -> [Pad015]
  FullyConstrained = true
  MakeInternals = false
  MapMode = 5
  Placement = pos=(0,41,0) rot=(1,0,0;1.5708rad)
  sketch-geometry (4):
    g0: LineSegment StartX=23 StartY=23 StartZ=0 EndX=71 EndY=3 EndZ=0
    g1: LineSegment StartX=71 StartY=3 StartZ=0 EndX=23 EndY=3 EndZ=0
    g2: LineSegment StartX=23 StartY=3 StartZ=0 EndX=23 EndY=23 EndZ=0
    g3: LineSegment [constr] StartX=23 StartY=23 StartZ=0 EndX=23 EndY=43 EndZ=0
  constraints (9):
    c: PointOnObject(g0,g-3)
    c: Coincident(g0,g1)
    c: Coincident(g1,g-3)
    c: Coincident(g1,g2)
    c: Coincident(g2,g0)
    c: Coincident(g3,g0)
    c: Coincident(g3,g-3)
    c: Equal(g3,g2)
    c: Coincident(g0,g-4)
FEATURE [PartDesign::Pad] Pad016  label="P-Stepperwippe -Steppercase 1"
  BaseFeature = -> Pad015
  Direction = (0,-1,2e-16)
  Length = 3
  Length2 = 10
  Profile = -> Sketch022
  ReferenceAxis = -> Sketch022 [N_Axis]
  Refine = true
  Reversed = true
  Suppressed = false
  Type = 0
FEATURE [Sketcher::SketchObject] Sketch023  label="Sk-Stepperwippe - Frontstrebe rechts"
  ArcFitTolerance = 1e-06
  AttachmentSupport = -> [Pad016]
  ExternalGeometry = -> [Pad016]
  FullyConstrained = true
  MakeInternals = false
  MapMode = 5
  Placement = pos=(0,90,6.543e-13) rot=(0,0.707107,0.707107;3.14159rad)
  sketch-geometry (4):
    g0: LineSegment [constr] StartX=-23 StartY=43 StartZ=0 EndX=-23 EndY=23 EndZ=0
    g1: LineSegment StartX=-23 StartY=23 StartZ=0 EndX=-71 EndY=3 EndZ=0
    g2: LineSegment StartX=-71 StartY=3 StartZ=0 EndX=-23 EndY=3 EndZ=0
    g3: LineSegment StartX=-23 StartY=3 StartZ=0 EndX=-23 EndY=23 EndZ=0
  constraints (9):
    c: Coincident(g0,g-3)
    c: Coincident(g0,g1)
    c: Coincident(g1,g-4)
    c: Coincident(g1,g2)
    c: Coincident(g2,g-3)
    c: Coincident(g2,g3)
    c: Coincident(g3,g1)
    c: Vertical(g0)
    c: Equal(g0,g3)
FEATURE [PartDesign::Pad] Pad017  label="P-Stepperwippe -Steppercase 2"
  BaseFeature = -> Pad016
  Direction = (0,1,7.4e-15)
  Length = 3
  Length2 = 10
  Profile = -> Sketch023
  ReferenceAxis = -> Sketch023 [N_Axis]
  Refine = true
  Reversed = true
  Suppressed = false
  Type = 0
FEATURE [Sketcher::SketchObject] Sketch024  label="Sk-Stepperwippe - Bohrungen"
  ArcFitTolerance = 1e-06
  AttachmentSupport = -> [Pad017]
  ExternalGeometry = -> [Pad017]
  FullyConstrained = true
  MakeInternals = false
  MapMode = 5
  Placement = pos=(23,0,0) rot=(0.57735,0.57735,0.57735;2.0944rad)
  sketch-geometry (15):
    g0: LineSegment [constr] StartX=50 StartY=39.5 StartZ=0 EndX=50 EndY=8.5 EndZ=0
    g1: LineSegment [constr] StartX=50 StartY=8.5 StartZ=0 EndX=81 EndY=8.5 EndZ=0
    g2: LineSegment [constr] StartX=81 StartY=8.5 StartZ=0 EndX=81 EndY=39.5 EndZ=0
    g3: LineSegment [constr] StartX=81 StartY=39.5 StartZ=0 EndX=50 EndY=39.5 EndZ=0
    g4: LineSegment [constr] StartX=50 StartY=8.5 StartZ=0 EndX=50 EndY=3 EndZ=0
    g5: LineSegment [constr] StartX=44 StartY=3 StartZ=0 EndX=50 EndY=8.5 EndZ=0
    g6: LineSegment [constr] StartX=81 StartY=8.5 StartZ=0 EndX=87 EndY=3 EndZ=0
    g7: Circle CenterX=50 CenterY=39.5 CenterZ=0 NormalX=0 NormalY=0 NormalZ=1 AngleXU=0 Radius=2
    g8: Circle CenterX=81 CenterY=39.5 CenterZ=0 NormalX=0 NormalY=0 NormalZ=1 AngleXU=0 Radius=2
    g9: Circle CenterX=81 CenterY=8.5 CenterZ=0 NormalX=0 NormalY=0 NormalZ=1 AngleXU=0 Radius=2
    g10: Circle CenterX=50 CenterY=8.5 CenterZ=0 NormalX=0 NormalY=0 NormalZ=1 AngleXU=0 Radius=2
    g11: LineSegment [constr] StartX=50 StartY=8.5 StartZ=0 EndX=65.5 EndY=24 EndZ=0
    g12: LineSegment [constr] StartX=65.5 StartY=24 StartZ=0 EndX=81 EndY=39.5 EndZ=0
    g13: LineSegment [constr] StartX=65.5 StartY=24 StartZ=0 EndX=81 EndY=8.5 EndZ=0
    g14: Circle CenterX=65.5 CenterY=24 CenterZ=0 NormalX=0 NormalY=0 NormalZ=1 AngleXU=0 Radius=12
  constraints (36):
    c: Coincident(g0,g1)
    c: Coincident(g1,g2)
    c: Coincident(g2,g3)
    c: Coincident(g3,g0)
    c: Vertical(g0)
    c: Vertical(g2)
    c: Horizontal(g1)
    c: Horizontal(g3)
    c: Distance(g0,g2) = 31
    c: Equal(g3,g0)
    c: Coincident(g4,g0)
    c: PointOnObject(g4,g-4)
    c: Vertical(g4)
    c: Coincident(g5,g-4)
    c: Coincident(g5,g0)
    c: Coincident(g6,g1)
    c: Coincident(g6,g-4)
    c: Equal(g5,g6)
    c: DistanceY(g4,g4) = 5.5
    c: Diameter(g7) = 4
    c: Coincident(g7,g0)
    c: Coincident(g8,g2)
    c: Coincident(g9,g1)
    c: Coincident(g10,g0)
    c: Equal(g7,g8)
    c: Equal(g8,g9)
    c: Equal(g9,g10)
    c: Coincident(g11,g0)
    c: Coincident(g12,g11)
    c: Coincident(g12,g2)
    c: Coincident(g13,g11)
    c: Coincident(g13,g1)
    c: Equal(g11,g12)
    c: Equal(g12,g13)
    c: Diameter(g14) = 24
    c: Coincident(g14,g11)
FEATURE [PartDesign::Pocket] Pocket001  label="P-Stepperwippe -Steppercase gebohrt"
  BaseFeature = -> Pad017
  Direction = (-1,0,0)
  Length = 5
  Length2 = 5
  Profile = -> Sketch024
  ReferenceAxis = -> Sketch024 [N_Axis]
  Refine = true
  Suppressed = false
  Type = 2
FEATURE [Sketcher::SketchObject] Sketch025  label="Sk-Stepperwippe - Wellenlager"
  ArcFitTolerance = 1e-06
  AttachmentSupport = -> [Pocket001]
  ExternalGeometry = -> [Pocket001]
  FullyConstrained = true
  MakeInternals = false
  MapMode = 5
  Placement = pos=(-31,0,0) rot=(0.57735,-0.57735,-0.57735;2.0944rad)
  sketch-geometry (12):
    g0: ArcOfCircle CenterX=-65.5 CenterY=24 CenterZ=0 NormalX=0 NormalY=0 NormalZ=1 AngleXU=0 Radius=10 StartAngle=0.858822 EndAngle=4.38939
    g1: LineSegment StartX=-68.6741 StartY=14.5171 StartZ=0 EndX=-26.5393 EndY=0.413698 EndZ=0
    g2: Circle CenterX=-65.5 CenterY=24 CenterZ=0 NormalX=0 NormalY=0 NormalZ=1 AngleXU=0 Radius=2.8
    g3: LineSegment StartX=-58.9667 StartY=31.5707 StartZ=0 EndX=-27.2666 EndY=4.21463 EndZ=0
    g4: LineSegment [constr] StartX=-27.2666 StartY=4.21463 StartZ=0 EndX=-25.8591 EndY=3 EndZ=0
    g5: ArcOfCircle CenterX=-24 CenterY=8 CenterZ=0 NormalX=0 NormalY=0 NormalZ=1 AngleXU=0 Radius=5 StartAngle=4.00041 EndAngle=4.71239
    g6: LineSegment [constr] StartX=-24 StartY=3 StartZ=0 EndX=-25.8591 EndY=3 EndZ=0
    g7: LineSegment [constr] StartX=-24 StartY=3 StartZ=0 EndX=-24 EndY=0 EndZ=0
    g8: ArcOfCircle CenterX=-24 CenterY=8 CenterZ=0 NormalX=0 NormalY=0 NormalZ=1 AngleXU=0 Radius=8 StartAngle=4.38939 EndAngle=4.71239
    g9: LineSegment StartX=-24 StartY=3 StartZ=0 EndX=-19 EndY=3 EndZ=0
    g10: LineSegment StartX=-19 StartY=3 StartZ=0 EndX=-19 EndY=0 EndZ=0
    g11: LineSegment StartX=-19 StartY=0 StartZ=0 EndX=-24 EndY=0 EndZ=0
  constraints (28):
    c: Tangent(g1,g0) = -1.5708
    c: Diameter(g0) = 20
    c: Diameter(g2) = 5.6
    c: Coincident(g2,g0)
    c: Coincident(g3,g4)
    c: Parallel(g3,g4)
    c: Tangent(g5,g3) = -1.5708
    c: Radius(g5) = 5
    c: Tangent(g3,g0) = 1.5708
    c: Tangent(g6,g5) = 1.5708
    c: Coincident(g6,g4)
    c: Horizontal(g6)
    c: PointOnObject(g7,g5)
    c: Coincident(g8,g5)
    c: Coincident(g8,g7)
    c: Tangent(g8,g1) = -1.5708
    c: Perpendicular(g8,g7)
    c: Coincident(g0,g-3)
    c: Coincident(g7,g-4)
    c: Coincident(g7,g-4)
    c: Coincident(g9,g5)
    c: Horizontal(g9)
    c: Coincident(g10,g9)
    c: PointOnObject(g10,g-1)
    c: Vertical(g10)
    c: Coincident(g11,g10)
    c: Coincident(g11,g7)
    c: DistanceX(g9,g9) = 5
FEATURE [PartDesign::Pad] Pad018  label="P-Stepperwippe - Case und Wellenlager"
  BaseFeature = -> Pocket001
  Direction = (-1,0,0)
  Length = 10
  Length2 = 10
  Profile = -> Sketch025
  ReferenceAxis = -> Sketch025 [N_Axis]
  Refine = true
  Reversed = true
  Suppressed = false
  Type = 0
FEATURE [Sketcher::SketchObject] Sketch026  label="Sk-Stepperwippe - Scharnierlager"
  ArcFitTolerance = 1e-06
  AttachmentSupport = -> [Pad018]
  ExternalGeometry = -> [Pad018]
  FullyConstrained = true
  MakeInternals = false
  MapMode = 5
  Placement = pos=(-31,0,0) rot=(0.57735,-0.57735,-0.57735;2.0944rad)
  sketch-geometry (3):
    g0: ArcOfCircle CenterX=4.77493 CenterY=5.3 CenterZ=0 NormalX=0 NormalY=0 NormalZ=1 AngleXU=0 Radius=5.3 StartAngle=3.59048 EndAngle=4.71239
    g1: LineSegment StartX=0 StartY=9e-16 StartZ=0 EndX=4.77493 EndY=9e-16 EndZ=0
    g2: LineSegment StartX=0 StartY=9e-16 StartZ=0 EndX=6.2e-15 EndY=3 EndZ=0
  constraints (7):
    c: Radius(g0) = 5.3
    c: Coincident(g1,g-1)
    c: Horizontal(g1)
    c: Tangent(g1,g0) = -1.5708
    c: Coincident(g2,g1)
    c: Coincident(g2,g-3)
    c: Coincident(g2,g0)
FEATURE [PartDesign::Pad] Pad019  label="P-Stepperwippe - Case und Wellenlager - Scharnier 1"
  BaseFeature = -> Pad018
  Direction = (-1,0,0)
  Length = 10
  Length2 = 10
  Profile = -> Sketch026
  ReferenceAxis = -> Sketch026 [N_Axis]
  Refine = true
  Reversed = true
  Suppressed = false
  Type = 3
  UpToFace = -> Pad018 [Face7]
FEATURE [Sketcher::SketchObject] Sketch027  label="Sk-Stepperwippe - Scharnier links"
  ArcFitTolerance = 1e-06
  AttachmentOffset = pos=(0,0,-20.25) rot=(0,0,1;0rad)
  AttachmentSupport = -> [Pad019]
  ExternalGeometry = -> [Pad019]
  FullyConstrained = true
  MakeInternals = false
  MapMode = 5
  Placement = pos=(-10.75,0,0) rot=(0.57735,-0.57735,-0.57735;2.0944rad)
  sketch-geometry (5):
    g0: Circle CenterX=4.77493 CenterY=5.3 CenterZ=0 NormalX=0 NormalY=0 NormalZ=1 AngleXU=0 Radius=3.3
    g1: LineSegment StartX=4.77493 StartY=9e-16 StartZ=0 EndX=4.77493 EndY=0.3 EndZ=0
    g2: ArcOfCircle CenterX=4.77493 CenterY=5.3 CenterZ=0 NormalX=0 NormalY=0 NormalZ=1 AngleXU=0 Radius=5.3 StartAngle=3.59048 EndAngle=4.71239
    g3: ArcOfCircle CenterX=4.77493 CenterY=5.3 CenterZ=0 NormalX=0 NormalY=0 NormalZ=1 AngleXU=0 Radius=5 StartAngle=4.71239 EndAngle=9.72596
    g4: LineSegment StartX=8e-15 StartY=3 StartZ=0 EndX=8e-15 EndY=3.81676 EndZ=0
  constraints (13):
    c: Diameter(g0) = 6.6
    c: Coincident(g1,g-3)
    c: Coincident(g2,g0)
    c: Coincident(g2,g1)
    c: Coincident(g3,g0)
    c: Coincident(g3,g1)
    c: Diameter(g3) = 10
    c: Coincident(g0,g-3)
    c: Coincident(g4,g2)
    c: Coincident(g4,g3)
    c: Vertical(g4)
    c: PointOnObject(g2,g-4)
    c: Vertical(g1)
FEATURE [PartDesign::Pad] Pad020  label="P-Stepperwippe - Case und Wellenlager - Scharnier 2"
  BaseFeature = -> Pad019
  Direction = (-1,0,0)
  Length = 20
  Length2 = 10
  Profile = -> Sketch027
  ReferenceAxis = -> Sketch027 [N_Axis]
  Refine = true
  Reversed = true
  Suppressed = false
  Type = 0
FEATURE [Sketcher::SketchObject] Sketch028  label="Sk-Stepperwippe - Scharnier rechts"
  ArcFitTolerance = 1e-06
  AttachmentOffset = pos=(0,0,-20.25) rot=(0,0,1;0rad)
  AttachmentSupport = -> [Pad020]
  ExternalGeometry = -> [Pad020]
  FullyConstrained = true
  MakeInternals = false
  MapMode = 5
  Placement = pos=(50.75,0,0) rot=(0.57735,0.57735,0.57735;2.0944rad)
  sketch-geometry (5):
    g0: Circle CenterX=-4.77493 CenterY=5.3 CenterZ=0 NormalX=0 NormalY=0 NormalZ=1 AngleXU=0 Radius=3.3
    g1: ArcOfCircle CenterX=-4.77493 CenterY=5.3 CenterZ=0 NormalX=0 NormalY=0 NormalZ=1 AngleXU=0 Radius=5 StartAngle=5.982 EndAngle=10.9956
    g2: ArcOfCircle CenterX=-4.77493 CenterY=5.3 CenterZ=0 NormalX=0 NormalY=0 NormalZ=1 AngleXU=0 Radius=5.3 StartAngle=4.71239 EndAngle=5.8343
    g3: LineSegment StartX=-4.77493 StartY=0.3 StartZ=0 EndX=-4.77493 EndY=9e-16 EndZ=0
    g4: LineSegment StartX=-6.6915e-12 StartY=3.81676 StartZ=0 EndX=-6.6915e-12 EndY=3 EndZ=0
  constraints (12):
    c: Coincident(g1,g0)
    c: Equal(g0,g-3)
    c: Coincident(g0,g2)
    c: Coincident(g0,g-5)
    c: Coincident(g1,g-4)
    c: Coincident(g3,g1)
    c: Coincident(g3,g2)
    c: Coincident(g2,g-5)
    c: PointOnObject(g1,g-6)
    c: Coincident(g4,g1)
    c: Coincident(g4,g2)
    c: Vertical(g4)
FEATURE [PartDesign::Pad] Pad021  label="P-Stepperwippe - Case und Wellenlager - Scharnier 3"
  BaseFeature = -> Pad020
  Direction = (1,0,0)
  Length = 20
  Length2 = 10
  Profile = -> Sketch028
  ReferenceAxis = -> Sketch028 [N_Axis]
  Refine = true
  Reversed = true
  Suppressed = false
  Type = 0
FEATURE [Sketcher::SketchObject] Sketch029  label="Sk-Stepperwippe - Wellenlager Federhaken"
  ArcFitTolerance = 1e-06
  AttachmentOffset = pos=(0,0,-3) rot=(0,0,1;0rad)
  AttachmentSupport = -> [Pad021]
  ExternalGeometry = -> [Pad021]
  FullyConstrained = false
  MakeInternals = false
  MapMode = 5
  Placement = pos=(-28,0,0) rot=(0.57735,-0.57735,-0.57735;2.0944rad)
  sketch-geometry (10):
    g0: LineSegment StartX=-24 StartY=0 StartZ=0 EndX=-24 EndY=3 EndZ=0
    g1: LineSegment StartX=-24 StartY=3 StartZ=0 EndX=-44 EndY=3 EndZ=0
    g2: LineSegment StartX=-44 StartY=3 StartZ=0 EndX=-44 EndY=0 EndZ=0
    g3: LineSegment StartX=-44 StartY=0 StartZ=0 EndX=-24 EndY=0 EndZ=0
    g4: LineSegment StartX=-50.5622 StartY=8.45468 StartZ=0 EndX=-50.5622 EndY=11.4547 EndZ=0
    g5: LineSegment StartX=-50.5622 StartY=11.4547 StartZ=0 EndX=-70.5622 EndY=11.4547 EndZ=0
    g6: LineSegment StartX=-70.5622 StartY=11.4547 StartZ=0 EndX=-70.5622 EndY=8.45468 EndZ=0
    g7: LineSegment StartX=-70.5622 StartY=8.45468 StartZ=0 EndX=-50.5622 EndY=8.45468 EndZ=0
    g8: LineSegment [constr] StartX=-65.5 StartY=24 StartZ=0 EndX=-65.5 EndY=13.4547 EndZ=0
    g9: LineSegment [constr] StartX=-65.5 StartY=13.4547 StartZ=0 EndX=-65.5 EndY=11.4547 EndZ=0
  constraints (27):
    c: Coincident(g0,g1)
    c: Coincident(g1,g2)
    c: Coincident(g2,g3)
    c: Coincident(g3,g0)
    c: Vertical(g0)
    c: Vertical(g2)
    c: Horizontal(g1)
    c: Horizontal(g3)
    c: Distance(g0,g2) = 20
    c: Distance(g1,g3) = 3
    c: Coincident(g0,g-4)
    c: Coincident(g4,g5)
    c: Coincident(g5,g6)
    c: Coincident(g6,g7)
    c: Coincident(g7,g4)
    c: Vertical(g4)
    c: Vertical(g6)
    c: Horizontal(g5)
    c: Horizontal(g7)
    c: Coincident(g8,g-5)
    c: PointOnObject(g9,g5)
    c: Coincident(g8,g9)
    c: Vertical(g8)
    c: Vertical(g9)
    c: PointOnObject(g8,g-3)
    c: DistanceY(g9,g9) = 2
    c: PointOnObject(g4,g-3)
FEATURE [PartDesign::Pad] Pad022  label="P-Stepperwippe - Mit Federhaken am Wellenlager 1"
  BaseFeature = -> Pad021
  Direction = (-1,0,0)
  Length = 4
  Length2 = 10
  Profile = -> Sketch029
  ReferenceAxis = -> Sketch029 [N_Axis]
  Refine = true
  Reversed = true
  Suppressed = false
  Type = 0
FEATURE [PartDesign::Fillet] Fillet001  label="P-Stepperwippe - Mit Federhaken am Wellenlager 2"
  Base = -> Pad022 [Edge187,Edge189,Edge193,Edge181]
  BaseFeature = -> Pad022
  Radius = 1
  Refine = true
  SupportTransform = false
  Suppressed = false
  UseAllEdges = false
FEATURE [Sketcher::SketchObject] Sketch030  label="Sk-Stepperwippe - Wellenlager Kopfzylinder M5"
  ArcFitTolerance = 1e-06
  AttachmentSupport = -> [Pad018]
  ExternalGeometry = -> [Pad018]
  FullyConstrained = true
  MakeInternals = false
  MapMode = 5
  Placement = pos=(-31,0,0) rot=(0.57735,-0.57735,-0.57735;2.0944rad)
  sketch-geometry (1):
    g0: Circle CenterX=-65.5 CenterY=24 CenterZ=0 NormalX=0 NormalY=0 NormalZ=1 AngleXU=0 Radius=4.6
  constraints (2):
    c: Diameter(g0) = 9.2
    c: Coincident(g0,g-3)
FEATURE [PartDesign::Pocket] Pocket002  label="P-Stepperwippe - Case und Wellenlager mit versenkter Schraube"
  BaseFeature = -> Fillet001
  Direction = (1,0,0)
  Length = 6
  Length2 = 5
  Profile = -> Sketch030
  ReferenceAxis = -> Sketch030 [N_Axis]
  Refine = true
  Suppressed = false
  Type = 0
FEATURE [Sketcher::SketchObject] Sketch031  label="Sk-Stepperwippe - Stepper Federhaken"
  ArcFitTolerance = 1e-06
  AttachmentSupport = -> [Pocket002]
  ExternalGeometry = -> [Pocket002]
  FullyConstrained = true
  MakeInternals = false
  MapMode = 5
  Placement = pos=(71,0,0) rot=(0.57735,0.57735,0.57735;2.0944rad)
  sketch-geometry (11):
    g0: LineSegment [constr] StartX=65.5 StartY=24 StartZ=0 EndX=65.5 EndY=3 EndZ=0
    g1: LineSegment StartX=63.5 StartY=3 StartZ=0 EndX=63.5 EndY=0 EndZ=0
    g2: LineSegment StartX=63.5 StartY=0 StartZ=0 EndX=67.5 EndY=0 EndZ=0
    g3: LineSegment StartX=67.5 StartY=0 StartZ=0 EndX=67.5 EndY=3 EndZ=0
    g4: LineSegment StartX=67.5 StartY=3 StartZ=0 EndX=63.5 EndY=3 EndZ=0
    g5: LineSegment StartX=40.5 StartY=3 StartZ=0 EndX=40.5 EndY=0 EndZ=0
    g6: LineSegment StartX=40.5 StartY=0 StartZ=0 EndX=44.5 EndY=0 EndZ=0
    g7: LineSegment StartX=44.5 StartY=0 StartZ=0 EndX=44.5 EndY=3 EndZ=0
    g8: LineSegment StartX=41 StartY=3 StartZ=0 EndX=40.5 EndY=3 EndZ=0
    g9: LineSegment StartX=44.5 StartY=3 StartZ=0 EndX=44 EndY=3 EndZ=0
    g10: LineSegment StartX=44 StartY=3 StartZ=0 EndX=41 EndY=3 EndZ=0
  constraints (30):
    c: Coincident(g0,g-3)
    c: Vertical(g0)
    c: Coincident(g1,g2)
    c: Coincident(g2,g3)
    c: Coincident(g3,g4)
    c: Coincident(g4,g1)
    c: Vertical(g1)
    c: Vertical(g3)
    c: Horizontal(g2)
    c: Horizontal(g4)
    c: Distance(g1,g3) = 4
    c: PointOnObject(g1,g-4)
    c: PointOnObject(g2,g-5)
    c: Symmetric(g1,g3,g0)
    c: Coincident(g8,g5)
    c: Coincident(g5,g6)
    c: Coincident(g6,g7)
    c: Coincident(g7,g9)
    c: Horizontal(g6)
    c: Vertical(g5)
    c: Vertical(g7)
    c: PointOnObject(g5,g-5)
    c: Equal(g7,g1)
    c: Coincident(g10,g8)
    c: Horizontal(g8)
    c: Coincident(g9,g10)
    c: Coincident(g9,g-6)
    c: Coincident(g8,g-6)
    c: Equal(g8,g9)
    c: Equal(g6,g2)
FEATURE [PartDesign::Pad] Pad023  label="P-Stepperwippe - Mit Federhaken 1"
  BaseFeature = -> Pocket002
  Direction = (1,0,0)
  Length = 7
  Length2 = 10
  Profile = -> Sketch031
  ReferenceAxis = -> Sketch031 [N_Axis]
  Refine = true
  Suppressed = false
  Type = 0
FEATURE [Sketcher::SketchObject] Sketch032  label="Sk-Stepperwippe - Stepper Federhakenhaken"
  ArcFitTolerance = 1e-06
  AttachmentSupport = -> [Pad023]
  ExternalGeometry = -> [Pad023]
  FullyConstrained = true
  MakeInternals = false
  MapMode = 5
  Placement = pos=(1.94e-14,-6.6e-15,3) rot=(0,0,1;0rad)
  sketch-geometry (8):
    g0: LineSegment StartX=78 StartY=40.5 StartZ=0 EndX=78 EndY=44.5 EndZ=0
    g1: LineSegment StartX=78 StartY=44.5 StartZ=0 EndX=74 EndY=44.5 EndZ=0
    g2: LineSegment StartX=74 StartY=44.5 StartZ=0 EndX=74 EndY=40.5 EndZ=0
    g3: LineSegment StartX=74 StartY=40.5 StartZ=0 EndX=78 EndY=40.5 EndZ=0
    g4: LineSegment StartX=78 StartY=67.5 StartZ=0 EndX=74 EndY=67.5 EndZ=0
    g5: LineSegment StartX=74 StartY=67.5 StartZ=0 EndX=74 EndY=63.5 EndZ=0
    g6: LineSegment StartX=74 StartY=63.5 StartZ=0 EndX=78 EndY=63.5 EndZ=0
    g7: LineSegment StartX=78 StartY=63.5 StartZ=0 EndX=78 EndY=67.5 EndZ=0
  constraints (20):
    c: Coincident(g0,g1)
    c: Coincident(g1,g2)
    c: Coincident(g2,g3)
    c: Coincident(g3,g0)
    c: Vertical(g2)
    c: Horizontal(g1)
    c: Horizontal(g3)
    c: Coincident(g0,g-4)
    c: Coincident(g4,g5)
    c: Coincident(g5,g6)
    c: Vertical(g5)
    c: Horizontal(g4)
    c: Horizontal(g6)
    c: Coincident(g4,g-3)
    c: Coincident(g0,g-4)
    c: Equal(g0,g3)
    c: Equal(g3,g6)
    c: Coincident(g7,g6)
    c: Coincident(g7,g4)
    c: Coincident(g6,g-3)
FEATURE [PartDesign::Pad] Pad024  label="P-Stepperwippe - Mit Federhaken 2"
  BaseFeature = -> Pad023
  Direction = (6.5e-15,-2.2e-15,1)
  Length = 3
  Length2 = 10
  Profile = -> Sketch032
  ReferenceAxis = -> Sketch032 [N_Axis]
  Refine = true
  Suppressed = false
  Type = 0
FEATURE [PartDesign::Fillet] Fillet002  label="P-Stepperwippe - komplett"
  Base = -> Pad024 [Edge160,Edge162,Edge159,Edge157,Edge222,Edge248,Edge247,Edge221,Edge219,Edge218,Edge246,Edge245]
  BaseFeature = -> Pad024
  Radius = 1.6
  Refine = true
  SupportTransform = false
  Suppressed = false
  UseAllEdges = false
FEATURE [PartDesign::Body] Body026  label="B-Stepperwippe"
  AllowCompound = false
  Group = -> [Sketch020,Pad014,Sketch021,Pad015,Sketch022,Pad016,Sketch023,Pad017,Sketch024,Pocket001,Sketch025,Pad018,Sketch026,Pad019,Sketch027,Pad020,Sketch028,Pad021,Sketch029,Pad022,Fillet001,Sketch030,Pocket002,Sketch031,Pad023,Sketch032,Pad024,Fillet002]
  Origin = -> Origin016
  Tip = -> Fillet002
FEATURE [Part::Feature] Body027  label="S-Stepperwippe"
  shape: bbox 109 x 99.77 x 46 mm, 102 faces (baked)
FEATURE [Mesh::Feature] Mesh004  label="M-Stepperwippe"
FEATURE [Part::FeaturePython] Screw012  label="M5x10-Schraube"  # WARN: FeaturePython — macro-defined, semantics opaque (R4)
  Diameter = 5
  Invert = false
  LeftHanded = false
  Length = 1
  LengthCustom = 10
  MatchOuter = false
  OffsetAngle = 0
  Placement = pos=(-26,65.5,24) rot=(0,1,0;4.71239rad)
  Thread = false
  Type = 53
FEATURE [Part::Feature] Body028  label="P-Feder 9x35 10"
  Placement = pos=(76,17.9828,-23.1543) rot=(1,0,0;5.49779rad)
  shape: bbox 14.35 x 31.53 x 32.61 mm, 13 faces (baked)
FEATURE [Part::Feature] Body029  label="P-Feder 9x35 11"
  Placement = pos=(-26,15.1543,-21.7401) rot=(1,0,0;5.49779rad)
  shape: bbox 14.35 x 31.53 x 32.61 mm, 13 faces (baked)
FEATURE [Sketcher::SketchObject] Sketch033  label="Sk-Stepperwippenscharnier - Boden"
  ArcFitTolerance = 1e-06
  AttachmentSupport = -> [XY_Plane018]
  FullyConstrained = true
  MakeInternals = false
  MapMode = 5
  sketch-geometry (12):
    g0: LineSegment StartX=-51 StartY=-5.3 StartZ=0 EndX=-51 EndY=-25.3 EndZ=0
    g1: LineSegment StartX=-51 StartY=-25.3 StartZ=0 EndX=51 EndY=-25.3 EndZ=0
    g2: LineSegment StartX=51 StartY=-25.3 StartZ=0 EndX=51 EndY=-5.3 EndZ=0
    g3: LineSegment StartX=51 StartY=-5.3 StartZ=0 EndX=-51 EndY=-5.3 EndZ=0
    g4: LineSegment [constr] StartX=-51 StartY=0 StartZ=0 EndX=-51 EndY=-5.3 EndZ=0
    g5: LineSegment [constr] StartX=-51 StartY=-15.3 StartZ=0 EndX=-36 EndY=-15.3 EndZ=0
    g6: LineSegment [constr] StartX=36 StartY=-15.3 StartZ=0 EndX=51 EndY=-15.3 EndZ=0
    g7: LineSegment [constr] StartX=-36 StartY=-15.3 StartZ=0 EndX=0 EndY=-15.3 EndZ=0
    g8: LineSegment [constr] StartX=0 StartY=-15.3 StartZ=0 EndX=36 EndY=-15.3 EndZ=0
    g9: Circle CenterX=-36 CenterY=-15.3 CenterZ=0 NormalX=0 NormalY=0 NormalZ=1 AngleXU=0 Radius=2.5
    g10: Circle CenterX=0 CenterY=-15.3 CenterZ=0 NormalX=0 NormalY=0 NormalZ=1 AngleXU=0 Radius=2.5
    g11: Circle CenterX=36 CenterY=-15.3 CenterZ=0 NormalX=0 NormalY=0 NormalZ=1 AngleXU=0 Radius=2.5
  constraints (32):
    c: Coincident(g0,g1)
    c: Coincident(g1,g2)
    c: Coincident(g2,g3)
    c: Coincident(g3,g0)
    c: Vertical(g0)
    c: Vertical(g2)
    c: Horizontal(g3)
    c: Symmetric(g0,g1,g-2)
    c: DistanceX(g1,g1) = 102
    c: DistanceY(g2,g2) = 20
    c: PointOnObject(g4,g-1)
    c: Coincident(g4,g0)
    c: Vertical(g4)
    c: DistanceY(g4,g4) = 5.3
    c: Coincident(g5,g7)
    c: Coincident(g8,g6)
    c: Symmetric(g0,g0,g5)
    c: Coincident(g7,g8)
    c: PointOnObject(g6,g2)
    c: Equal(g5,g6)
    c: Equal(g7,g8)
    c: Horizontal(g5)
    c: Horizontal(g8)
    c: Horizontal(g7)
    c: Horizontal(g6)
    c: DistanceX(g6,g6) = 15
    c: Coincident(g9,g5)
    c: Coincident(g10,g7)
    c: Coincident(g11,g6)
    c: Equal(g9,g10)
    c: Equal(g10,g11)
    c: Diameter(g9) = 5
FEATURE [PartDesign::Pad] Pad025  label="P-Stepperwippenscharnier Boden"
  Direction = (0,0,1)
  Length = 3
  Length2 = 10
  Profile = -> Sketch033
  ReferenceAxis = -> Sketch033 [N_Axis]
  Refine = true
  Suppressed = false
  Type = 0
FEATURE [Sketcher::SketchObject] Sketch034  label="Sk-Stepperwippenscharnier - Lager"
  ArcFitTolerance = 1e-06
  AttachmentSupport = -> [Pad025]
  ExternalGeometry = -> [Pad025]
  FullyConstrained = true
  MakeInternals = false
  MapMode = 5
  Placement = pos=(-51,0,0) rot=(0.57735,-0.57735,-0.57735;2.0944rad)
  sketch-geometry (3):
    g0: ArcOfCircle CenterX=0.525065 CenterY=5.3 CenterZ=0 NormalX=0 NormalY=0 NormalZ=1 AngleXU=0 Radius=5.3 StartAngle=4.71239 EndAngle=5.8343
    g1: LineSegment StartX=0.525065 StartY=0 StartZ=0 EndX=5.3 EndY=0 EndZ=0
    g2: LineSegment StartX=5.3 StartY=0 StartZ=0 EndX=5.3 EndY=3 EndZ=0
  constraints (7):
    c: Coincident(g0,g-3)
    c: Coincident(g1,g-3)
    c: Coincident(g2,g1)
    c: Coincident(g2,g0)
    c: Horizontal(g1)
    c: Diameter(g0) = 10.6
    c: Tangent(g1,g0) = -1.5708
FEATURE [PartDesign::Pad] Pad026  label="P-Stepperwippenscharnier mit Lager"
  BaseFeature = -> Pad025
  Direction = (-1,0,0)
  Length = 10
  Length2 = 10
  Profile = -> Sketch034
  ReferenceAxis = -> Sketch034 [N_Axis]
  Refine = true
  Reversed = true
  Suppressed = false
  Type = 3
  UpToFace = -> Pad025 [Face3]
FEATURE [Sketcher::SketchObject] Sketch035  label="Sk-Stepperwippenscharnier - Öse links"
  ArcFitTolerance = 1e-06
  AttachmentSupport = -> [Pad026]
  ExternalGeometry = -> [Pad026]
  FullyConstrained = true
  MakeInternals = false
  MapMode = 5
  Placement = pos=(-51,0,0) rot=(0.57735,-0.57735,-0.57735;2.0944rad)
  sketch-geometry (5):
    g0: Circle CenterX=0.525065 CenterY=5.3 CenterZ=0 NormalX=0 NormalY=0 NormalZ=1 AngleXU=0 Radius=3.2
    g1: ArcOfCircle CenterX=0.525065 CenterY=5.3 CenterZ=0 NormalX=0 NormalY=0 NormalZ=1 AngleXU=0 Radius=5 StartAngle=5.982 EndAngle=10.9956
    g2: ArcOfCircle CenterX=0.525065 CenterY=5.3 CenterZ=0 NormalX=0 NormalY=0 NormalZ=1 AngleXU=0 Radius=5.3 StartAngle=4.71239 EndAngle=5.8343
    g3: LineSegment StartX=5.3 StartY=3 StartZ=0 EndX=5.3 EndY=3.81676 EndZ=0
    g4: LineSegment StartX=0.525065 StartY=0 StartZ=0 EndX=0.525065 EndY=0.3 EndZ=0
  constraints (13):
    c: Diameter(g0) = 6.4
    c: Coincident(g0,g-3)
    c: Coincident(g1,g0)
    c: Coincident(g2,g0)
    c: Coincident(g2,g-3)
    c: PointOnObject(g2,g-4)
    c: Coincident(g3,g2)
    c: Coincident(g3,g1)
    c: Vertical(g3)
    c: Diameter(g1) = 10
    c: Coincident(g4,g2)
    c: Coincident(g4,g1)
    c: Vertical(g4)
FEATURE [PartDesign::Pad] Pad027  label="P-Stepperwippenscharnier Öse links"
  BaseFeature = -> Pad026
  Direction = (-1,0,0)
  Length = 19.75
  Length2 = 10
  Profile = -> Sketch035
  ReferenceAxis = -> Sketch035 [N_Axis]
  Refine = true
  Reversed = true
  Suppressed = false
  Type = 0
FEATURE [Sketcher::SketchObject] Sketch036  label="Sk-Stepperwippenscharnier - Öse rechts"
  ArcFitTolerance = 1e-06
  AttachmentSupport = -> [Pad027]
  ExternalGeometry = -> [Pad027]
  FullyConstrained = true
  MakeInternals = false
  MapMode = 5
  Placement = pos=(51,0,0) rot=(0.57735,0.57735,0.57735;2.0944rad)
  sketch-geometry (5):
    g0: Circle CenterX=-0.525065 CenterY=5.3 CenterZ=0 NormalX=0 NormalY=0 NormalZ=1 AngleXU=0 Radius=3.2
    g1: ArcOfCircle CenterX=-0.525065 CenterY=5.3 CenterZ=0 NormalX=0 NormalY=0 NormalZ=1 AngleXU=0 Radius=5 StartAngle=4.71239 EndAngle=9.72596
    g2: ArcOfCircle CenterX=-0.525065 CenterY=5.3 CenterZ=0 NormalX=0 NormalY=0 NormalZ=1 AngleXU=0 Radius=5.3 StartAngle=3.59048 EndAngle=4.71239
    g3: LineSegment StartX=-0.525065 StartY=0 StartZ=0 EndX=-0.525065 EndY=0.3 EndZ=0
    g4: LineSegment StartX=-5.3 StartY=3 StartZ=0 EndX=-5.3 EndY=3.81676 EndZ=0
  constraints (13):
    c: Coincident(g0,g-3)
    c: Equal(g0,g-5)
    c: Coincident(g1,g0)
    c: Coincident(g2,g0)
    c: Coincident(g2,g-3)
    c: PointOnObject(g2,g-4)
    c: Coincident(g3,g2)
    c: Coincident(g3,g1)
    c: Vertical(g3)
    c: Coincident(g4,g2)
    c: Coincident(g4,g1)
    c: Vertical(g4)
    c: Equal(g-6,g1)
FEATURE [PartDesign::Pad] Pad028  label="P-Stepperwippenscharnier Ösen aussen"
  BaseFeature = -> Pad027
  Direction = (1,0,0)
  Length = 19.75
  Length2 = 10
  Profile = -> Sketch036
  ReferenceAxis = -> Sketch036 [N_Axis]
  Refine = true
  Reversed = true
  Suppressed = false
  Type = 0
FEATURE [Sketcher::SketchObject] Sketch037  label="Sk-Stepperwippenscharnier - Öse mitte"
  ArcFitTolerance = 1e-06
  AttachmentOffset = pos=(0,0,21) rot=(0,0,1;0rad)
  AttachmentSupport = -> [Pad028]
  ExternalGeometry = -> [Pad028]
  FullyConstrained = true
  MakeInternals = false
  MapMode = 5
  Placement = pos=(-10.25,0,0) rot=(0.57735,0.57735,0.57735;2.0944rad)
  sketch-geometry (5):
    g0: ArcOfCircle CenterX=-0.525065 CenterY=5.3 CenterZ=0 NormalX=0 NormalY=0 NormalZ=1 AngleXU=0 Radius=5 StartAngle=4.71239 EndAngle=9.72596
    g1: ArcOfCircle CenterX=-0.525065 CenterY=5.3 CenterZ=0 NormalX=0 NormalY=0 NormalZ=1 AngleXU=0 Radius=5.3 StartAngle=3.59048 EndAngle=4.71239
    g2: LineSegment StartX=-5.3 StartY=3.81676 StartZ=0 EndX=-5.3 EndY=3 EndZ=0
    g3: Circle CenterX=-0.525065 CenterY=5.3 CenterZ=0 NormalX=0 NormalY=0 NormalZ=1 AngleXU=0 Radius=2.7
    g4: LineSegment StartX=-0.525065 StartY=0.3 StartZ=0 EndX=-0.525065 EndY=0 EndZ=0
  constraints (13):
    c: Coincident(g0,g-3)
    c: PointOnObject(g0,g-3)
    c: Coincident(g1,g-4)
    c: Coincident(g1,g-4)
    c: PointOnObject(g0,g-5)
    c: Coincident(g2,g0)
    c: Coincident(g2,g1)
    c: Vertical(g2)
    c: Coincident(g3,g1)
    c: Equal(g0,g-3)
    c: Coincident(g4,g0)
    c: Coincident(g4,g1)
    c: Diameter(g3) = 5.4
FEATURE [PartDesign::Pad] Pad029  label="P-Stepperwippenscharnier mit Ösen"
  BaseFeature = -> Pad028
  Direction = (1,0,0)
  Length = 20.5
  Length2 = 10
  Profile = -> Sketch037
  ReferenceAxis = -> Sketch037 [N_Axis]
  Refine = true
  Suppressed = false
  Type = 0
FEATURE [Sketcher::SketchObject] Sketch038  label="Sk-Stepperwippenscharnier - Gewindeloch"
  ArcFitTolerance = 1e-06
  AttachmentSupport = -> [Pad029]
  ExternalGeometry = -> [Pad029]
  FullyConstrained = true
  MakeInternals = false
  MapMode = 5
  Placement = pos=(10.25,0,0) rot=(0.57735,0.57735,0.57735;2.0944rad)
  sketch-geometry (1):
    g0: Circle CenterX=-0.525065 CenterY=5.3 CenterZ=0 NormalX=0 NormalY=0 NormalZ=1 AngleXU=0 Radius=2.7
  constraints (2):
    c: Coincident(g0,g-3)
    c: Equal(g0,g-3)
FEATURE [PartDesign::Hole] Hole001  label="P-Stepperwippenscharnier roh"
  BaseFeature = -> Pad029
  CustomThreadClearance = 0
  Depth = 25
  DepthType = 0
  Diameter = 5
  DrillForDepth = false
  DrillPoint = 1
  DrillPointAngle = 118
  HoleCutCountersinkAngle = 90
  HoleCutCustomValues = false
  HoleCutDepth = 0
  HoleCutDiameter = 6.1
  HoleCutType = 0
  ModelThread = true
  Profile = -> Sketch038
  Refine = true
  Suppressed = false
  Tapered = false
  TaperedAngle = 90
  ThreadClass = 5
  ThreadDepth = 25
  ThreadDepthType = 0
  ThreadDirection = 0
  ThreadFit = 0
  ThreadSize = 14
  ThreadType = 1
  Threaded = true
  UseCustomThreadClearance = false
FEATURE [Sketcher::SketchObject] Sketch039  label="Sk-Stepperwippenscharnier - Schraubensenkungen"
  ArcFitTolerance = 1e-06
  AttachmentSupport = -> [Hole001]
  ExternalGeometry = -> [Hole001]
  FullyConstrained = true
  MakeInternals = false
  MapMode = 5
  Placement = pos=(0,0,3) rot=(0,0,1;0rad)
  sketch-geometry (3):
    g0: Circle CenterX=-36 CenterY=-15.3 CenterZ=0 NormalX=0 NormalY=0 NormalZ=1 AngleXU=0 Radius=2.5
    g1: Circle CenterX=0 CenterY=-15.3 CenterZ=0 NormalX=0 NormalY=0 NormalZ=1 AngleXU=0 Radius=2.5
    g2: Circle CenterX=36 CenterY=-15.3 CenterZ=0 NormalX=0 NormalY=0 NormalZ=1 AngleXU=0 Radius=2.5
  constraints (6):
    c: Coincident(g0,g-4)
    c: Equal(g0,g-4)
    c: Coincident(g1,g-3)
    c: Equal(g1,g-3)
    c: Coincident(g2,g-5)
    c: Equal(g2,g-5)
FEATURE [PartDesign::Hole] Hole002  label="P-Stepperwippenscharnier"
  BaseFeature = -> Hole001
  CustomThreadClearance = 0
  Depth = 25
  DepthType = 0
  Diameter = 5
  DrillForDepth = false
  DrillPoint = 1
  DrillPointAngle = 118
  HoleCutCountersinkAngle = 90
  HoleCutCustomValues = false
  HoleCutDepth = 0
  HoleCutDiameter = 9
  HoleCutType = 2
  ModelThread = false
  Profile = -> Sketch039
  Refine = true
  Suppressed = false
  Tapered = false
  TaperedAngle = 90
  ThreadClass = 0
  ThreadDepth = 25
  ThreadDepthType = 0
  ThreadDirection = 0
  ThreadFit = 0
  ThreadSize = 0
  ThreadType = 0
  Threaded = false
  UseCustomThreadClearance = false
FEATURE [PartDesign::Body] Body030  label="B-Stepperwippenscharnier"
  AllowCompound = false
  Group = -> [Sketch033,Pad025,Sketch034,Pad026,Sketch035,Pad027,Sketch036,Pad028,Sketch037,Pad029,Sketch038,Hole001,Sketch039,Hole002]
  Origin = -> Origin018
  Placement = pos=(20,-4.25,0) rot=(0,0,1;0rad)
  Tip = -> Hole002
FEATURE [Part::Feature] Body031  label="S-Stepperwippenscharnier"
  Placement = pos=(20,-8.13173,1.07071) rot=(1,0,0;5.49779rad)
  shape: bbox 102 x 26.27 x 20.89 mm, 94 faces (baked)
FEATURE [Mesh::Feature] Mesh005  label="M-Stepperwippenscharnier"
FEATURE [Part::FeaturePython] Screw013  label="M6x50-Schraube links"  # WARN: FeaturePython — macro-defined, semantics opaque (R4)
  Diameter = 8
  Invert = false
  LeftHanded = false
  Length = 4
  LengthCustom = 50
  MatchOuter = false
  OffsetAngle = 0
  Placement = pos=(-31,-4.74704,5.33942) rot=(-0.519988,-0.677661,0.519988;1.95044rad)
  Thread = true
  Type = 65
FEATURE [Part::FeaturePython] Screw014  label="M6x50-Schraube rechts"  # WARN: FeaturePython — macro-defined, semantics opaque (R4)
  Diameter = 8
  Invert = false
  LeftHanded = false
  Length = 4
  LengthCustom = 50
  MatchOuter = false
  OffsetAngle = 0
  Placement = pos=(71,-4.74704,5.33942) rot=(0.621515,0.476905,0.621515;2.25159rad)
  Thread = true
  Type = 65
FEATURE [Part::FeaturePython] Screw015  label="#8x16-Schraube"  # WARN: FeaturePython — macro-defined, semantics opaque (R4)
  Diameter = 9
  Invert = false
  LeftHanded = false
  Length = 13
  LengthCustom = 16
  MatchOuter = false
  OffsetAngle = 0
  Placement = pos=(56,-16.8,14.2024) rot=(1,0,0;5.49779rad)
  Thread = false
  Type = 15
FEATURE [Part::FeaturePython] Screw016  label="#8x16-Schraube005"  # WARN: FeaturePython — macro-defined, semantics opaque (R4)
  Diameter = 9
  Invert = false
  LeftHanded = false
  Length = 13
  LengthCustom = 16
  MatchOuter = false
  OffsetAngle = 0
  Placement = pos=(-16,-16.8,14.2024) rot=(1,0,0;5.49779rad)
  Thread = false
  Type = 15
FEATURE [Part::FeaturePython] Screw017  label="#8x16-Schraube006"  # WARN: FeaturePython — macro-defined, semantics opaque (R4)
  Diameter = 9
  Invert = false
  LeftHanded = false
  Length = 13
  LengthCustom = 16
  MatchOuter = false
  OffsetAngle = 0
  Placement = pos=(19.9,-16.8,14.2024) rot=(1,0,0;5.49779rad)
  Thread = false
  Type = 15
FEATURE [App::Part] Part005  label="Antrieb"
  Group = -> [Body027,Body031,Part,Screw012,Body028,Body029,Screw013,Screw014,Screw015,Screw016,Screw017]
  Origin = -> Origin017
  Placement = pos=(0,-68.976,4.94975) rot=(-1,0,0;5.49779rad)
FEATURE [App::Part] Part002  label="Drehgestell"
  Group = -> [Body010,Part001,Part005]
  Origin = -> Origin009
  Placement = pos=(0,0,30) rot=(0,0,1;0rad)
FEATURE [Assembly::AssemblyObject] Assembly  label="Rotationstrieb"
  Group = -> [Joints,Body009,Part002,GroundedJoint]
  Origin = -> Origin003
  Type = Assembly
FEATURE [Sketcher::SketchObject] Sketch040  label="Sk-Walzenzylinder red."
  ArcFitTolerance = 1e-06
  AttachmentSupport = -> [XY_Plane019]
  FullyConstrained = true
  MakeInternals = false
  MapMode = 5
  sketch-geometry (2):
    g0: Circle CenterX=0 CenterY=0 CenterZ=0 NormalX=0 NormalY=0 NormalZ=1 AngleXU=0 Radius=9
    g1: Circle CenterX=0 CenterY=0 CenterZ=0 NormalX=0 NormalY=0 NormalZ=1 AngleXU=0 Radius=2
  constraints (4):
    c: Diameter(g0) = 18
    c: Coincident(g0,g-1)
    c: Coincident(g1,g0)
    c: Diameter(g1) = 4
FEATURE [PartDesign::Pad] Pad030  label="P-Walzenzylinder red."
  Direction = (0,0,1)
  Length = 40
  Length2 = 10
  Profile = -> Sketch040
  ReferenceAxis = -> Sketch040 [N_Axis]
  Refine = true
  Suppressed = false
  Type = 0
FEATURE [Sketcher::SketchObject] Sketch041  label="Sk-Wellenfeder red."
  ArcFitTolerance = 1e-06
  AttachmentSupport = -> [Pad030]
  FullyConstrained = true
  MakeInternals = false
  MapMode = 5
  Placement = pos=(0,0,0) rot=(1,0,0;3.14159rad)
  sketch-geometry (7):
    g0: LineSegment StartX=-2.14942 StartY=4.45 StartZ=0 EndX=-2.14942 EndY=1.55 EndZ=0
    g1: LineSegment [constr] StartX=-2.14942 StartY=1.55 StartZ=0 EndX=2.14942 EndY=1.55 EndZ=0
    g2: LineSegment StartX=2.14942 StartY=1.55 StartZ=0 EndX=2.14942 EndY=4.45 EndZ=0
    g3: LineSegment [constr] StartX=0 StartY=1.55 StartZ=0 EndX=0 EndY=-2.65 EndZ=0
    g4: LineSegment StartX=2.14942 StartY=4.45 StartZ=0 EndX=1.14646e-11 EndY=4.45 EndZ=0
    g5: LineSegment StartX=1.14646e-11 StartY=4.45 StartZ=0 EndX=-2.14942 EndY=4.45 EndZ=0
    g6: ArcOfCircle CenterX=0 CenterY=0 CenterZ=0 NormalX=0 NormalY=0 NormalZ=1 AngleXU=0 Radius=2.65 StartAngle=2.51683 EndAngle=6.90795
  constraints (22):
    c: Coincident(g0,g1)
    c: Coincident(g1,g2)
    c: Coincident(g2,g4)
    c: Coincident(g5,g0)
    c: Vertical(g0)
    c: Vertical(g2)
    c: Horizontal(g1)
    c: Vertical(g3)
    c: PointOnObject(g-1,g3)
    c: Coincident(g4,g5)
    c: Horizontal(g4)
    c: Horizontal(g5)
    c: Equal(g5,g4)
    c: PointOnObject(g3,g1)
    c: DistanceY(g3,g3) = 4.2
    c: DistanceY(g2,g2) = 2.9
    c: DistanceX(g1,g1) = 4.29884
    c: Coincident(g6,g-1)
    c: Coincident(g6,g0)
    c: Coincident(g6,g1)
    c: Diameter(g6) = 5.3
    c: PointOnObject(g3,g6)
FEATURE [Sketcher::SketchObject] Sketch042  label="Sk-Antriebswalzenhülle_18.0-20.0"
  ArcFitTolerance = 1e-06
  AttachmentSupport = -> [XY_Plane020]
  FullyConstrained = true
  MakeInternals = false
  MapMode = 5
  sketch-geometry (2):
    g0: Circle CenterX=0 CenterY=0 CenterZ=0 NormalX=0 NormalY=0 NormalZ=1 AngleXU=0 Radius=8.7
    g1: Circle CenterX=0 CenterY=0 CenterZ=0 NormalX=0 NormalY=0 NormalZ=1 AngleXU=0 Radius=10
  constraints (4):
    c: Diameter(g0) = 17.4
    c: Coincident(g0,g-1)
    c: Diameter(g1) = 20
    c: Coincident(g1,g0)
FEATURE [PartDesign::Pad] Pad032  label="P-Antriebswalzenhülle_18.0-20.0"
  Direction = (0,0,1)
  Length = 40
  Length2 = 10
  Profile = -> Sketch042
  ReferenceAxis = -> Sketch042 [N_Axis]
  Refine = true
  Suppressed = false
  Type = 0
FEATURE [PartDesign::Body] Body033  label="B-Antriebswalzenhülle_18.0-20.0"
  AllowCompound = false
  Group = -> [Sketch042,Pad032]
  Origin = -> Origin020
  Tip = -> Pad032
FEATURE [Mesh::Feature] Mesh006  label="M-Antriebswalze-NEMA17_18.0_Feder"
FEATURE [PartDesign::Pocket] Pocket003  label="P-Wellenfedernut"
  BaseFeature = -> Pad030
  Direction = (0,0,1)
  Length = 25
  Length2 = 5
  Profile = -> Sketch041
  ReferenceAxis = -> Sketch041 [N_Axis]
  Refine = true
  Suppressed = false
  Type = 0
FEATURE [Sketcher::SketchObject] Sketch043  label="Sk-Wellenachsenbohrung"
  ArcFitTolerance = 1e-06
  AttachmentSupport = -> [Pocket003]
  ExternalGeometry = -> [Pocket003]
  FullyConstrained = true
  MakeInternals = false
  MapMode = 5
  Placement = pos=(0,0,40) rot=(0,0,1;0rad)
  sketch-geometry (1):
    g0: Circle CenterX=0 CenterY=0 CenterZ=0 NormalX=0 NormalY=0 NormalZ=1 AngleXU=0 Radius=2
  constraints (2):
    c: Coincident(g0,g-1)
    c: Equal(g0,g-3)
FEATURE [PartDesign::Hole] Hole003  label="P-Wellenachsengewinde"
  BaseFeature = -> Pocket003
  CustomThreadClearance = 0
  Depth = 20
  DepthType = 0
  Diameter = 4.224
  DrillForDepth = false
  DrillPoint = 1
  DrillPointAngle = 118
  HoleCutCountersinkAngle = 90
  HoleCutCustomValues = false
  HoleCutDepth = 0
  HoleCutDiameter = 6.1
  HoleCutType = 0
  ModelThread = true
  Profile = -> Sketch043
  Refine = true
  Suppressed = false
  Tapered = false
  TaperedAngle = 90
  ThreadClass = 0
  ThreadDepth = 20
  ThreadDepthType = 1
  ThreadDirection = 0
  ThreadFit = 0
  ThreadSize = 13
  ThreadType = 1
  Threaded = true
  UseCustomThreadClearance = false
FEATURE [Sketcher::SketchObject] Sketch044  label="Sk-Antriebswalzenwellenfeder Profil"
  ArcFitTolerance = 1e-06
  AttachmentSupport = -> [XY_Plane021]
  FullyConstrained = true
  MakeInternals = false
  MapMode = 5
  sketch-geometry (7):
    g0: LineSegment StartX=0 StartY=0 StartZ=0 EndX=20.7 EndY=0 EndZ=0
    g1: LineSegment StartX=22 StartY=1.3 StartZ=0 EndX=22 EndY=2.6 EndZ=0
    g2: LineSegment StartX=22 StartY=2.6 StartZ=0 EndX=0 EndY=3.2 EndZ=0
    g3: LineSegment StartX=0 StartY=3.2 StartZ=0 EndX=0 EndY=0 EndZ=0
    g4: GeomPoint [constr] X=22 Y=2.6 Z=0
    g5: ArcOfCircle CenterX=20.7 CenterY=1.3 CenterZ=0 NormalX=0 NormalY=0 NormalZ=1 AngleXU=0 Radius=1.3 StartAngle=4.71239 EndAngle=6.28319
    g6: GeomPoint [constr] X=22 Y=0 Z=0
  constraints (17):
    c: Coincident(g2,g3)
    c: Coincident(g3,g0)
    c: Horizontal(g0)
    c: Vertical(g1)
    c: Vertical(g3)
    c: Coincident(g0,g-1)
    c: DistanceX(g0,g6) = 22
    c: DistanceY(g3,g3) = 3.2
    c: DistanceY(g6,g4) = 2.6
    c: PointOnObject(g4,g2)
    c: PointOnObject(g4,g1)
    c: Coincident(g1,g2)
    c: PointOnObject(g6,g1)
    c: PointOnObject(g6,g0)
    c: Tangent(g1,g5) = -1.5708
    c: Tangent(g0,g5) = -1.5708
    c: Radius(g5) = 1.3
FEATURE [PartDesign::Pad] Pad033  label="P-Antriebswalzenwellenfeder"
  Direction = (0,0,1)
  Length = 4
  Length2 = 10
  Profile = -> Sketch044
  ReferenceAxis = -> Sketch044 [N_Axis]
  Refine = true
  Suppressed = false
  Type = 0
FEATURE [PartDesign::Body] Body034  label="B-Antriebswalzenwellenfeder"
  AllowCompound = false
  Group = -> [Sketch044,Pad033]
  Origin = -> Origin021
  Placement = pos=(2,-1.8,22) rot=(0.707107,0,-0.707107;3.14159rad)
  Tip = -> Pad033
FEATURE [Sketcher::SketchObject] Sketch045  label="Sk-Wellenfederkeil Profil"
  ArcFitTolerance = 1e-06
  AttachmentSupport = -> [Hole003]
  ExternalGeometry = -> [Hole003]
  FullyConstrained = true
  MakeInternals = false
  MapMode = 5
  Placement = pos=(2.14942,0,0) rot=(0.57735,-0.57735,-0.57735;2.0944rad)
  sketch-geometry (3):
    g0: LineSegment StartX=4.45 StartY=0 StartZ=0 EndX=5.15 EndY=25 EndZ=0
    g1: LineSegment StartX=5.15 StartY=25 StartZ=0 EndX=4.45 EndY=25 EndZ=0
    g2: LineSegment StartX=4.45 StartY=25 StartZ=0 EndX=4.45 EndY=0 EndZ=0
  constraints (7):
    c: Coincident(g0,g1)
    c: Coincident(g1,g2)
    c: Horizontal(g1)
    c: Coincident(g-3,g1)
    c: Coincident(g0,g2)
    c: Coincident(g0,g-3)
    c: DistanceX(g1,g1) = 0.7
FEATURE [PartDesign::Pocket] Pocket004  label="P-Walzenzylinder komplett"
  BaseFeature = -> Hole003
  Direction = (1,0,0)
  Length = 0
  Length2 = 5
  Profile = -> Sketch045
  ReferenceAxis = -> Sketch045 [N_Axis]
  Refine = true
  Reversed = true
  Suppressed = false
  Type = 3
  UpToFace = -> Hole003 [Face7]
FEATURE [PartDesign::Body] Body032  label="B-Antriebswalze-NEMA17_18.0"
  AllowCompound = false
  Group = -> [Sketch040,Pad030,Sketch041,Pocket003,Sketch043,Hole003,Sketch045,Pocket004]
  Origin = -> Origin019
  Tip = -> Pocket004
FEATURE [App::DocumentObjectGroup] Group001  label="Bodies"
  Group = -> [Body,Body004,Body006,Body008,Body001,Body011,Body012,Body018,Body026,Body030,Body032,Body033,Body034]
FEATURE [Mesh::Feature] Mesh007  label="M-Antriebswalze-NEMA17_18.0_Nut"
FEATURE [Mesh::Feature] Mesh008  label="M-Antriebswalzenhülle_18.0-20.0"
FEATURE [Mesh::Feature] Mesh009  label="M-Antriebswalzenwellenfeder"
FEATURE [App::DocumentObjectGroup] Group  label="Meshes"
  Group = -> [Mesh,Mesh002,Mesh003,Mesh004,Mesh005,Mesh006,Mesh009,Mesh007,Mesh008]
